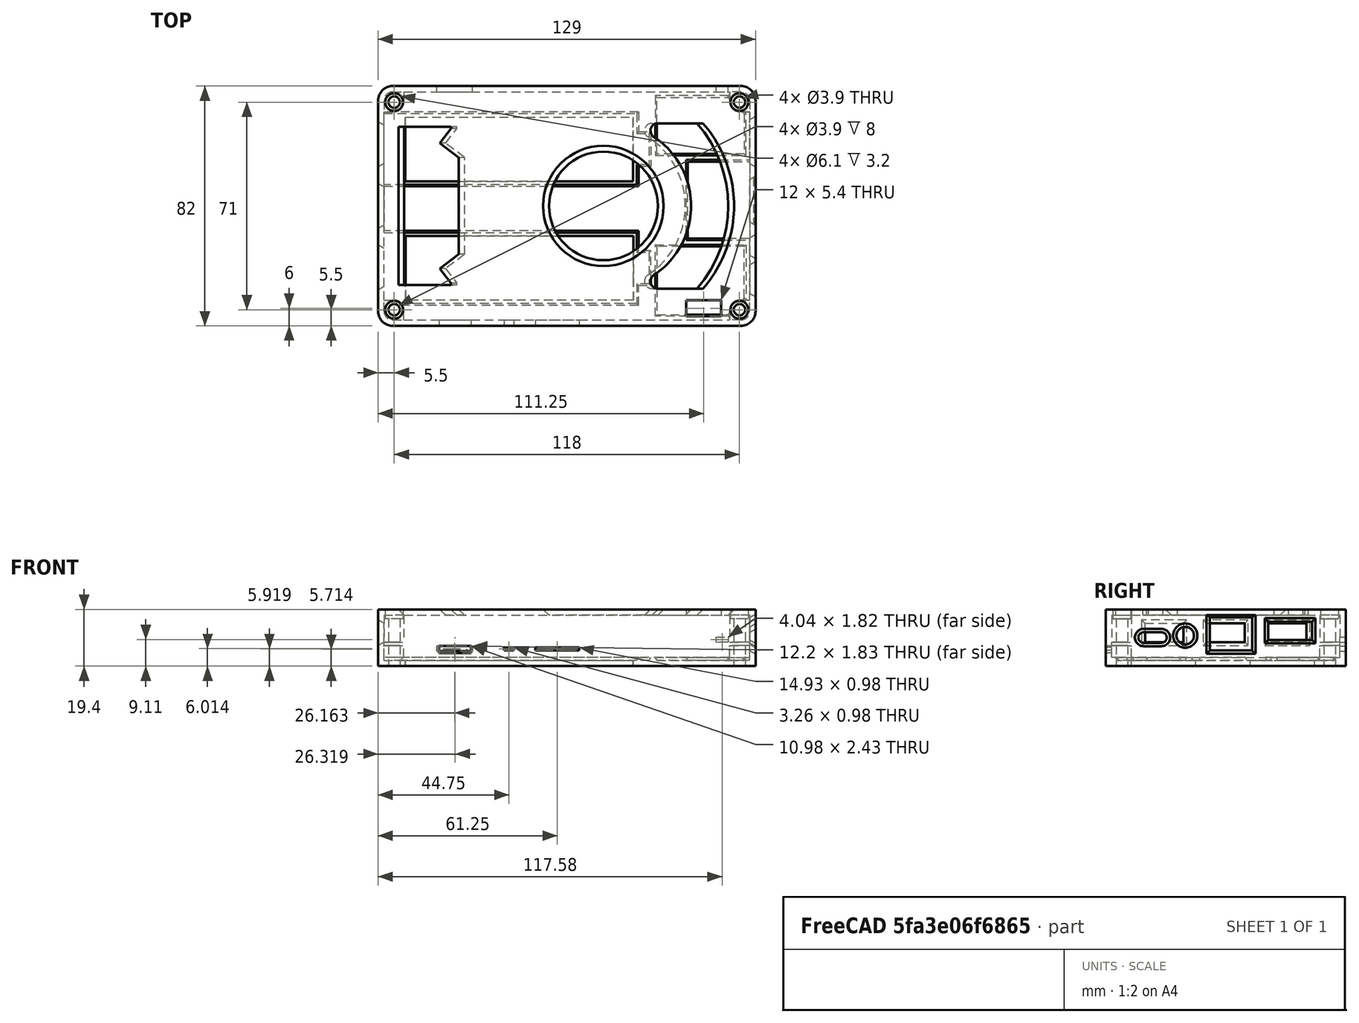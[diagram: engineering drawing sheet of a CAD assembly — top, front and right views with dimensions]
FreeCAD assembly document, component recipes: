
FREECAD ASSEMBLY — COMPONENT RECIPES ("case")

This assembly document has 10 components, labeled P0..P9 below (a component is one placed body or linked part). 4 of them carry a construction recipe — the FreeCAD feature program that regenerates the part from scratch, quoted from this document or its linked companion documents; the rest are supplied as boundary geometry only. No exploded tour is included for this assembly.
COMPONENT P0 — recipe-attached ("Parent", modeled in this document).
Construction recipe (the document's own serialized feature program — sketch geometry with constraints, then the solid features built on it; lengths are millimeters unless a unit is written):

FEATURE [Sketcher::SketchObject] Sketch  label="sketch_base"
  FullyConstrained = true
  MapMode = 5
  Support = -> [XY_Plane]
  expr: .Constraints.long_side = <<data>>.lattepanda_long + <<data>>.padding * 2
  expr: .Constraints.radius = <<data>>.lattepanda_radius
  expr: .Constraints.short_side = <<data>>.lattepanda_short + <<data>>.padding * 2
  sketch-geometry (10):
    g0: ArcOfCircle CenterX=-59.5 CenterY=36 CenterZ=0 NormalX=0 NormalY=0 NormalZ=1 AngleXU=0 Radius=3 StartAngle=1.5708 EndAngle=3.14159
    g1: LineSegment StartX=-59.5 StartY=39 StartZ=0 EndX=59.5 EndY=39 EndZ=0
    g2: ArcOfCircle CenterX=59.5 CenterY=36 CenterZ=0 NormalX=0 NormalY=0 NormalZ=1 AngleXU=0 Radius=3 StartAngle=2.097e-13 EndAngle=1.5708
    g3: LineSegment StartX=62.5 StartY=36 StartZ=0 EndX=62.5 EndY=-36 EndZ=0
    g4: ArcOfCircle CenterX=59.5 CenterY=-36 CenterZ=0 NormalX=0 NormalY=0 NormalZ=1 AngleXU=0 Radius=3 StartAngle=4.71239 EndAngle=6.28319
    g5: LineSegment StartX=59.5 StartY=-39 StartZ=0 EndX=-59.5 EndY=-39 EndZ=0
    g6: ArcOfCircle CenterX=-59.5 CenterY=-36 CenterZ=0 NormalX=0 NormalY=0 NormalZ=1 AngleXU=0 Radius=3 StartAngle=3.14159 EndAngle=4.71239
    g7: LineSegment StartX=-62.5 StartY=-36 StartZ=0 EndX=-62.5 EndY=36 EndZ=0
    g8: GeomPoint X=-62.5 Y=39 Z=0
    g9: GeomPoint X=62.5 Y=-39 Z=0
  constraints (23):
    c: Tangent(g0,g1) = 1.5708
    c: Tangent(g1,g2) = 1.5708
    c: Tangent(g2,g3) = 1.5708
    c: Tangent(g3,g4) = 1.5708
    c: Tangent(g4,g5) = 1.5708
    c: Tangent(g5,g6) = 1.5708
    c: Tangent(g6,g7) = 1.5708
    c: Tangent(g7,g0) = 1.5708
    c: Horizontal(g1)
    c: Horizontal(g5)
    c: Vertical(g3)
    c: Vertical(g7)
    c: Equal(g0,g2)
    c: Equal(g2,g4)
    c: Equal(g4,g6)
    c: PointOnObject(g8,g1)
    c: PointOnObject(g8,g7)
    c: PointOnObject(g9,g3)
    c: PointOnObject(g9,g5)
    c: DistanceY(g5,g0) = 78  'short_side'
    c: DistanceX(g0,g2) = 125  'long_side'
    c: Radius(g2) = 3  'radius'
    c: Symmetric(g0,g4,g-1)
FEATURE [PartDesign::Pad] Pad
  Direction = (0,0,1)
  Length = 15.4
  Length2 = 10
  Profile = -> Sketch
  ReferenceAxis = -> Sketch [N_Axis]
  Type = 0
  expr: Length = <<data>>.lattepanda_height
FEATURE [PartDesign::Thickness] Thickness
  Base = -> Pad [Face10]
  BaseFeature = -> Pad
  Intersection = false
  Join = 1
  Mode = 0
  SupportTransform = false
  Value = 2
  expr: Value = <<data>>.wall_thickness
FEATURE [Sketcher::SketchObject] Sketch003  label="sketch_screwhole_shafts"
  ExternalGeometry = -> [Thickness]
  FullyConstrained = true
  MapMode = 5
  Support = -> [XY_Plane]
  expr: Constraints[4] = <<data>>.screwhole_shaft_diameter + Spreadsheet.padding * 2
  expr: Constraints[68] = (<<data>>.screwhole_shaft_diameter + <<data>>.padding * 2) / 2
  expr: Constraints[8] = (<<data>>.screwhole_shaft_diameter + <<data>>.padding * 2) / 2
  sketch-geometry (24):
    g0: LineSegment StartX=-59.5 StartY=39 StartZ=0 EndX=-55.7 EndY=39 EndZ=0
    g1: LineSegment StartX=-62.5 StartY=36 StartZ=0 EndX=-62.5 EndY=32.2 EndZ=0
    g2: LineSegment StartX=-55.7 StartY=39 StartZ=0 EndX=-55.7 EndY=35.6 EndZ=0
    g3: ArcOfCircle CenterX=-59.1 CenterY=35.6 CenterZ=0 NormalX=0 NormalY=0 NormalZ=1 AngleXU=0 Radius=3.4 StartAngle=4.71239 EndAngle=6.28319
    g4: LineSegment StartX=-62.5 StartY=32.2 StartZ=0 EndX=-59.1 EndY=32.2 EndZ=0
    g5: LineSegment StartX=-59.5 StartY=-39 StartZ=0 EndX=-55.7 EndY=-39 EndZ=0
    g6: LineSegment StartX=-62.5 StartY=-36 StartZ=0 EndX=-62.5 EndY=-32.2 EndZ=0
    g7: LineSegment StartX=-55.7 StartY=-39 StartZ=0 EndX=-55.7 EndY=-35.6 EndZ=0
    g8: ArcOfCircle CenterX=-59.1 CenterY=-35.6 CenterZ=0 NormalX=0 NormalY=0 NormalZ=1 AngleXU=0 Radius=3.4 StartAngle=1e-15 EndAngle=1.5708
    g9: LineSegment StartX=-62.5 StartY=-32.2 StartZ=0 EndX=-59.1 EndY=-32.2 EndZ=0
    g10: LineSegment StartX=59.5 StartY=39 StartZ=0 EndX=55.7 EndY=39 EndZ=0
    g11: LineSegment StartX=62.5 StartY=36 StartZ=0 EndX=62.5 EndY=32.2 EndZ=0
    g12: LineSegment StartX=55.7 StartY=39 StartZ=0 EndX=55.7 EndY=35.6 EndZ=0
    g13: ArcOfCircle CenterX=59.1 CenterY=35.6 CenterZ=0 NormalX=0 NormalY=0 NormalZ=1 AngleXU=0 Radius=3.4 StartAngle=3.14159 EndAngle=4.71239
    g14: LineSegment StartX=62.5 StartY=32.2 StartZ=0 EndX=59.1 EndY=32.2 EndZ=0
    g15: LineSegment StartX=59.5 StartY=-39 StartZ=0 EndX=55.7 EndY=-39 EndZ=0
    g16: LineSegment StartX=62.5 StartY=-36 StartZ=0 EndX=62.5 EndY=-32.2 EndZ=0
    g17: LineSegment StartX=55.7 StartY=-39 StartZ=0 EndX=55.7 EndY=-35.6 EndZ=0
    g18: ArcOfCircle CenterX=59.1 CenterY=-35.6 CenterZ=0 NormalX=0 NormalY=0 NormalZ=1 AngleXU=0 Radius=3.4 StartAngle=1.5708 EndAngle=3.14159
    g19: LineSegment StartX=62.5 StartY=-32.2 StartZ=0 EndX=59.1 EndY=-32.2 EndZ=0
    g20: ArcOfCircle CenterX=-59.5 CenterY=-36 CenterZ=0 NormalX=0 NormalY=0 NormalZ=1 AngleXU=0 Radius=3 StartAngle=3.14159 EndAngle=4.71239
    g21: ArcOfCircle CenterX=-59.5 CenterY=36 CenterZ=0 NormalX=0 NormalY=0 NormalZ=1 AngleXU=0 Radius=3 StartAngle=1.5708 EndAngle=3.14159
    g22: ArcOfCircle CenterX=59.5 CenterY=36 CenterZ=0 NormalX=0 NormalY=0 NormalZ=1 AngleXU=0 Radius=3 StartAngle=2.113e-13 EndAngle=1.5708
    g23: ArcOfCircle CenterX=59.5 CenterY=-36 CenterZ=0 NormalX=0 NormalY=0 NormalZ=1 AngleXU=0 Radius=3 StartAngle=4.71239 EndAngle=6.28319
  constraints (72):
    c: Coincident(g0,g-3)
    c: Horizontal(g0)
    c: Coincident(g1,g-3)
    c: Vertical(g1)
    c: DistanceX(g1,g0) = 6.8
    c: Coincident(g2,g0)
    c: Vertical(g2)
    c: Coincident(g3,g2)
    c: Radius(g3) = 3.4
    c: Coincident(g4,g1)
    c: Coincident(g4,g3)
    c: Horizontal(g4)
    c: Equal(g1,g0)
    c: Equal(g4,g2)
    c: Horizontal(g5)
    c: Vertical(g6)
    c: Coincident(g7,g5)
    c: Vertical(g7)
    c: Coincident(g8,g7)
    c: Coincident(g9,g6)
    c: Coincident(g9,g8)
    c: Horizontal(g9)
    c: Equal(g6,g5)
    c: Equal(g9,g7)
    c: Coincident(g6,g-4)
    c: Coincident(g5,g-4)
    c: Equal(g6,g1)
    c: Equal(g9,g4)
    c: Horizontal(g10)
    c: Vertical(g11)
    c: Coincident(g12,g10)
    c: Vertical(g12)
    c: Coincident(g13,g12)
    c: Coincident(g14,g11)
    c: Coincident(g14,g13)
    c: Horizontal(g14)
    c: Equal(g11,g10)
    c: Equal(g14,g12)
    c: Horizontal(g15)
    c: Vertical(g16)
    c: Coincident(g17,g15)
    c: Vertical(g17)
    c: Coincident(g18,g17)
    c: Coincident(g19,g16)
    c: Coincident(g19,g18)
    c: Horizontal(g19)
    c: Equal(g16,g15)
    c: Equal(g19,g17)
    c: Equal(g16,g11)
    c: Equal(g19,g14)
    c: Coincident(g10,g-6)
    c: Coincident(g11,g-6)
    c: Coincident(g16,g-5)
    c: Coincident(g15,g-5)
    c: Equal(g10,g0)
    c: Coincident(g20,g-4)
    c: Coincident(g20,g5)
    c: Coincident(g20,g6)
    c: Coincident(g21,g-3)
    c: Coincident(g21,g1)
    c: Coincident(g21,g0)
    c: Coincident(g22,g-6)
    c: Coincident(g22,g10)
    c: Coincident(g22,g11)
    c: Coincident(g23,g-5)
    c: Coincident(g23,g16)
    c: Coincident(g23,g15)
    c: Equal(g17,g7)
    c: DistanceY(g2,g2) = 3.4
    c: Equal(g3,g13)
    c: Equal(g18,g8)
    c: Equal(g13,g18)
FEATURE [PartDesign::Pad] Pad001
  BaseFeature = -> Thickness
  Direction = (0,0,1)
  Length = 5
  Length2 = 10
  Profile = -> Sketch003
  ReferenceAxis = -> Sketch003 [N_Axis]
  Type = 0
  expr: Length = <<data>>.lattepanda_h_below
FEATURE [PartDesign::Body] Body  label="Parent"
  Group = -> [Sketch,Pad,Thickness,Sketch003,Pad001]
  Origin = -> Origin
  Tip = -> Pad001
COMPONENT P1 — recipe-attached ("case", modeled in this document).
Construction recipe (the document's own serialized feature program — sketch geometry with constraints, then the solid features built on it; lengths are millimeters unless a unit is written):

FEATURE [Sketcher::SketchObject] Sketch004  label="sketch_base001"
  FullyConstrained = true
  MapMode = 5
  Support = -> [XY_Plane]
  expr: .Constraints.long_side = <<data>>.lattepanda_long + <<data>>.padding * 2
  expr: .Constraints.radius = <<data>>.lattepanda_radius
  expr: .Constraints.short_side = <<data>>.lattepanda_short + <<data>>.padding * 2
  sketch-geometry (10):
    g0: ArcOfCircle CenterX=-59.5 CenterY=36 CenterZ=0 NormalX=0 NormalY=0 NormalZ=1 AngleXU=0 Radius=3 StartAngle=1.5708 EndAngle=3.14159
    g1: LineSegment StartX=-59.5 StartY=39 StartZ=0 EndX=59.5 EndY=39 EndZ=0
    g2: ArcOfCircle CenterX=59.5 CenterY=36 CenterZ=0 NormalX=0 NormalY=0 NormalZ=1 AngleXU=0 Radius=3 StartAngle=2.095e-13 EndAngle=1.5708
    g3: LineSegment StartX=62.5 StartY=36 StartZ=0 EndX=62.5 EndY=-36 EndZ=0
    g4: ArcOfCircle CenterX=59.5 CenterY=-36 CenterZ=0 NormalX=0 NormalY=0 NormalZ=1 AngleXU=0 Radius=3 StartAngle=4.71239 EndAngle=6.28319
    g5: LineSegment StartX=59.5 StartY=-39 StartZ=0 EndX=-59.5 EndY=-39 EndZ=0
    g6: ArcOfCircle CenterX=-59.5 CenterY=-36 CenterZ=0 NormalX=0 NormalY=0 NormalZ=1 AngleXU=0 Radius=3 StartAngle=3.14159 EndAngle=4.71239
    g7: LineSegment StartX=-62.5 StartY=-36 StartZ=0 EndX=-62.5 EndY=36 EndZ=0
    g8: GeomPoint X=-62.5 Y=39 Z=0
    g9: GeomPoint X=62.5 Y=-39 Z=0
  constraints (23):
    c: Tangent(g0,g1) = 1.5708
    c: Tangent(g1,g2) = 1.5708
    c: Tangent(g2,g3) = 1.5708
    c: Tangent(g3,g4) = 1.5708
    c: Tangent(g4,g5) = 1.5708
    c: Tangent(g5,g6) = 1.5708
    c: Tangent(g6,g7) = 1.5708
    c: Tangent(g7,g0) = 1.5708
    c: Horizontal(g1)
    c: Horizontal(g5)
    c: Vertical(g3)
    c: Vertical(g7)
    c: Equal(g0,g2)
    c: Equal(g2,g4)
    c: Equal(g4,g6)
    c: PointOnObject(g8,g1)
    c: PointOnObject(g8,g7)
    c: PointOnObject(g9,g3)
    c: PointOnObject(g9,g5)
    c: DistanceY(g5,g0) = 78  'short_side'
    c: DistanceX(g0,g2) = 125  'long_side'
    c: Radius(g2) = 3  'radius'
    c: Symmetric(g0,g4,g-1)
FEATURE [PartDesign::Pad] Pad002
  Direction = (0,0,1)
  Length = 15.4
  Length2 = 10
  Profile = -> Sketch004
  ReferenceAxis = -> Sketch004 [N_Axis]
  Type = 0
  expr: Length = <<data>>.lattepanda_height
FEATURE [PartDesign::Thickness] Thickness001
  Base = -> Pad002 [Face10]
  BaseFeature = -> Pad002
  Intersection = false
  Join = 1
  Mode = 0
  SupportTransform = false
  Value = 2
  expr: Value = <<data>>.wall_thickness
FEATURE [Sketcher::SketchObject] Sketch005  label="sketch_screwhole_shafts001"
  ExternalGeometry = -> [Thickness001]
  FullyConstrained = true
  MapMode = 5
  Support = -> [XY_Plane]
  expr: Constraints[4] = <<data>>.screwhole_shaft_diameter + Spreadsheet.padding * 2
  expr: Constraints[68] = (<<data>>.screwhole_shaft_diameter + <<data>>.padding * 2) / 2
  expr: Constraints[8] = (<<data>>.screwhole_shaft_diameter + <<data>>.padding * 2) / 2
  sketch-geometry (24):
    g0: LineSegment StartX=-59.5 StartY=39 StartZ=0 EndX=-55.7 EndY=39 EndZ=0
    g1: LineSegment StartX=-62.5 StartY=36 StartZ=0 EndX=-62.5 EndY=32.2 EndZ=0
    g2: LineSegment StartX=-55.7 StartY=39 StartZ=0 EndX=-55.7 EndY=35.6 EndZ=0
    g3: ArcOfCircle CenterX=-59.1 CenterY=35.6 CenterZ=0 NormalX=0 NormalY=0 NormalZ=1 AngleXU=0 Radius=3.4 StartAngle=4.71239 EndAngle=6.28319
    g4: LineSegment StartX=-62.5 StartY=32.2 StartZ=0 EndX=-59.1 EndY=32.2 EndZ=0
    g5: LineSegment StartX=-59.5 StartY=-39 StartZ=0 EndX=-55.7 EndY=-39 EndZ=0
    g6: LineSegment StartX=-62.5 StartY=-36 StartZ=0 EndX=-62.5 EndY=-32.2 EndZ=0
    g7: LineSegment StartX=-55.7 StartY=-39 StartZ=0 EndX=-55.7 EndY=-35.6 EndZ=0
    g8: ArcOfCircle CenterX=-59.1 CenterY=-35.6 CenterZ=0 NormalX=0 NormalY=0 NormalZ=1 AngleXU=0 Radius=3.4 StartAngle=-2.7e-15 EndAngle=1.5708
    g9: LineSegment StartX=-62.5 StartY=-32.2 StartZ=0 EndX=-59.1 EndY=-32.2 EndZ=0
    g10: LineSegment StartX=59.5 StartY=39 StartZ=0 EndX=55.7 EndY=39 EndZ=0
    g11: LineSegment StartX=62.5 StartY=36 StartZ=0 EndX=62.5 EndY=32.2 EndZ=0
    g12: LineSegment StartX=55.7 StartY=39 StartZ=0 EndX=55.7 EndY=35.6 EndZ=0
    g13: ArcOfCircle CenterX=59.1 CenterY=35.6 CenterZ=0 NormalX=0 NormalY=0 NormalZ=1 AngleXU=0 Radius=3.4 StartAngle=3.14159 EndAngle=4.71239
    g14: LineSegment StartX=62.5 StartY=32.2 StartZ=0 EndX=59.1 EndY=32.2 EndZ=0
    g15: LineSegment StartX=59.5 StartY=-39 StartZ=0 EndX=55.7 EndY=-39 EndZ=0
    g16: LineSegment StartX=62.5 StartY=-36 StartZ=0 EndX=62.5 EndY=-32.2 EndZ=0
    g17: LineSegment StartX=55.7 StartY=-39 StartZ=0 EndX=55.7 EndY=-35.6 EndZ=0
    g18: ArcOfCircle CenterX=59.1 CenterY=-35.6 CenterZ=0 NormalX=0 NormalY=0 NormalZ=1 AngleXU=0 Radius=3.4 StartAngle=1.5708 EndAngle=3.14159
    g19: LineSegment StartX=62.5 StartY=-32.2 StartZ=0 EndX=59.1 EndY=-32.2 EndZ=0
    g20: ArcOfCircle CenterX=-59.5 CenterY=-36 CenterZ=0 NormalX=0 NormalY=0 NormalZ=1 AngleXU=0 Radius=3 StartAngle=3.14159 EndAngle=4.71239
    g21: ArcOfCircle CenterX=-59.5 CenterY=36 CenterZ=0 NormalX=0 NormalY=0 NormalZ=1 AngleXU=0 Radius=3 StartAngle=1.5708 EndAngle=3.14159
    g22: ArcOfCircle CenterX=59.5 CenterY=36 CenterZ=0 NormalX=0 NormalY=0 NormalZ=1 AngleXU=0 Radius=3 StartAngle=2.089e-13 EndAngle=1.5708
    g23: ArcOfCircle CenterX=59.5 CenterY=-36 CenterZ=0 NormalX=0 NormalY=0 NormalZ=1 AngleXU=0 Radius=3 StartAngle=4.71239 EndAngle=6.28319
  constraints (72):
    c: Coincident(g0,g-3)
    c: Horizontal(g0)
    c: Coincident(g1,g-3)
    c: Vertical(g1)
    c: DistanceX(g1,g0) = 6.8
    c: Coincident(g2,g0)
    c: Vertical(g2)
    c: Coincident(g3,g2)
    c: Radius(g3) = 3.4
    c: Coincident(g4,g1)
    c: Coincident(g4,g3)
    c: Horizontal(g4)
    c: Equal(g1,g0)
    c: Equal(g4,g2)
    c: Horizontal(g5)
    c: Vertical(g6)
    c: Coincident(g7,g5)
    c: Vertical(g7)
    c: Coincident(g8,g7)
    c: Coincident(g9,g6)
    c: Coincident(g9,g8)
    c: Horizontal(g9)
    c: Equal(g6,g5)
    c: Equal(g9,g7)
    c: Coincident(g6,g-4)
    c: Coincident(g5,g-4)
    c: Equal(g6,g1)
    c: Equal(g9,g4)
    c: Horizontal(g10)
    c: Vertical(g11)
    c: Coincident(g12,g10)
    c: Vertical(g12)
    c: Coincident(g13,g12)
    c: Coincident(g14,g11)
    c: Coincident(g14,g13)
    c: Horizontal(g14)
    c: Equal(g11,g10)
    c: Equal(g14,g12)
    c: Horizontal(g15)
    c: Vertical(g16)
    c: Coincident(g17,g15)
    c: Vertical(g17)
    c: Coincident(g18,g17)
    c: Coincident(g19,g16)
    c: Coincident(g19,g18)
    c: Horizontal(g19)
    c: Equal(g16,g15)
    c: Equal(g19,g17)
    c: Equal(g16,g11)
    c: Equal(g19,g14)
    c: Coincident(g10,g-6)
    c: Coincident(g11,g-6)
    c: Coincident(g16,g-5)
    c: Coincident(g15,g-5)
    c: Equal(g10,g0)
    c: Coincident(g20,g-4)
    c: Coincident(g20,g5)
    c: Coincident(g20,g6)
    c: Coincident(g21,g-3)
    c: Coincident(g21,g1)
    c: Coincident(g21,g0)
    c: Coincident(g22,g-6)
    c: Coincident(g22,g10)
    c: Coincident(g22,g11)
    c: Coincident(g23,g-5)
    c: Coincident(g23,g16)
    c: Coincident(g23,g15)
    c: Equal(g17,g7)
    c: DistanceY(g2,g2) = 3.4
    c: Equal(g3,g13)
    c: Equal(g18,g8)
    c: Equal(g13,g18)
FEATURE [PartDesign::Pad] Pad003
  BaseFeature = -> Thickness001
  Direction = (0,0,1)
  Length = 5
  Length2 = 10
  Profile = -> Sketch005
  ReferenceAxis = -> Sketch005 [N_Axis]
  Type = 0
  expr: Length = <<data>>.lattepanda_h_below
FEATURE [Sketcher::SketchObject] Sketch007
  ExternalGeometry = -> [Feature]
  FullyConstrained = true
  MapMode = 5
  Placement = pos=(62.5,0,0) rot=(0.57735,-0.57735,-0.57735;2.0944rad)
  Support = -> [Pad003]
  sketch-geometry (24):
    g0: GeomPoint X=13.85 Y=8.45 Z=0
    g1: GeomPoint X=28.1 Y=7.78 Z=0
    g2: GeomPoint X=21.96 Y=7.78 Z=0
    g3: LineSegment StartX=21.96 StartY=9.58 StartZ=0 EndX=28.1 EndY=9.58 EndZ=0
    g4: LineSegment StartX=21.96 StartY=5.98 StartZ=0 EndX=28.1 EndY=5.98 EndZ=0
    g5: GeomPoint X=5.4559 Y=14.6873 Z=0
    g6: GeomPoint X=5.4559 Y=3.34 Z=0
    g7: GeomPoint X=-9.04069 Y=3.34 Z=0
    g8: GeomPoint X=-9.04069 Y=14.6873 Z=0
    g9: LineSegment StartX=5.4559 StartY=14.6873 StartZ=0 EndX=-9.04069 EndY=14.6873 EndZ=0
    g10: LineSegment StartX=-9.04069 StartY=3.34 StartZ=0 EndX=-9.04069 EndY=14.6873 EndZ=0
    g11: LineSegment StartX=-9.04069 StartY=3.34 StartZ=0 EndX=5.4559 EndY=3.34 EndZ=0
    g12: LineSegment StartX=5.4559 StartY=3.34 StartZ=0 EndX=5.4559 EndY=14.6873 EndZ=0
    g13: GeomPoint X=-14.5 Y=13.2209 Z=0
    g14: GeomPoint X=-14.5 Y=6.95627 Z=0
    g15: GeomPoint X=-29.5 Y=6.95627 Z=0
    g16: GeomPoint X=-29.5 Y=13.2209 Z=0
    g17: LineSegment StartX=-14.5 StartY=13.2209 StartZ=0 EndX=-29.5 EndY=13.2209 EndZ=0
    g18: LineSegment StartX=-29.5 StartY=13.2209 StartZ=0 EndX=-29.5 EndY=6.95627 EndZ=0
    g19: LineSegment StartX=-29.5 StartY=6.95627 StartZ=0 EndX=-14.5 EndY=6.95627 EndZ=0
    g20: LineSegment StartX=-14.5 StartY=6.95627 StartZ=0 EndX=-14.5 EndY=13.2209 EndZ=0
    g21: ArcOfCircle CenterX=21.96 CenterY=7.78 CenterZ=0 NormalX=0 NormalY=0 NormalZ=1 AngleXU=0 Radius=1.8 StartAngle=1.5708 EndAngle=4.71239
    g22: ArcOfCircle CenterX=28.1 CenterY=7.78 CenterZ=0 NormalX=0 NormalY=0 NormalZ=1 AngleXU=0 Radius=1.8 StartAngle=4.71239 EndAngle=7.85398
    g23: Circle CenterX=13.85 CenterY=8.45 CenterZ=0 NormalX=0 NormalY=0 NormalZ=1 AngleXU=0 Radius=3
  constraints (50):
    c: Symmetric(g-12,g-12,g0)
    c: Horizontal(g1,g2)
    c: Vertical(g2,g-17)
    c: Symmetric(g-15,g-14,g1)
    c: Horizontal(g3)
    c: Horizontal(g4)
    c: Equal(g4,g3)
    c: Horizontal(g5,g-5)
    c: Vertical(g5,g-3)
    c: Horizontal(g8,g-5)
    c: Vertical(g8,g-4)
    c: Vertical(g7,g-4)
    c: Vertical(g6,g-3)
    c: Horizontal(g6,g7)
    c: Horizontal(g7,g-6)
    c: Coincident(g9,g5)
    c: Coincident(g9,g8)
    c: Coincident(g10,g7)
    c: Coincident(g10,g9)
    c: Coincident(g11,g10)
    c: Coincident(g11,g6)
    c: Coincident(g12,g11)
    c: Coincident(g12,g9)
    c: Horizontal(g13,g-7)
    c: Horizontal(g-7,g16)
    c: Horizontal(g15,g-9)
    c: Horizontal(g-9,g14)
    c: Vertical(g13,g-8)
    c: Vertical(g-8,g14)
    c: Vertical(g16,g-10)
    c: Vertical(g-10,g15)
    c: Coincident(g17,g13)
    c: Coincident(g17,g16)
    c: Coincident(g18,g17)
    c: Coincident(g18,g15)
    c: Coincident(g19,g18)
    c: Coincident(g19,g14)
    c: Coincident(g20,g19)
    c: Coincident(g20,g17)
    c: Coincident(g21,g2)
    c: Coincident(g21,g4)
    c: Coincident(g21,g3)
    c: Coincident(g22,g1)
    c: Coincident(g22,g3)
    c: Coincident(g22,g4)
    c: Equal(g21,g22)
    c: Angle(g22) = 3.14159
    c: Radius(g22) = 1.8
    c: Coincident(g23,g0)
    c: Radius(g23) = 3
FEATURE [PartDesign::Pocket] Pocket
  BaseFeature = -> Pad003
  Direction = (1,0,0)
  Length = 5
  Length2 = 5
  Profile = -> Sketch007
  ReferenceAxis = -> Sketch007 [N_Axis]
  TaperAngle = 30
  Type = 0
FEATURE [Sketcher::SketchObject] Sketch009
  ExternalGeometry = -> [Feature]
  FullyConstrained = true
  MapMode = 5
  Placement = pos=(-62.5,0,0) rot=(0.57735,0.57735,0.57735;2.0944rad)
  Support = -> [Pocket]
  sketch-geometry (12):
    g0: LineSegment StartX=-27.6 StartY=12.6565 StartZ=0 EndX=-14.5 EndY=12.6565 EndZ=0
    g1: LineSegment StartX=-14.5 StartY=12.6565 StartZ=0 EndX=-14.5 EndY=6.2 EndZ=0
    g2: LineSegment StartX=-14.5 StartY=6.2 StartZ=0 EndX=-27.6 EndY=6.2 EndZ=0
    g3: LineSegment StartX=-27.6 StartY=6.2 StartZ=0 EndX=-27.6 EndY=12.6565 EndZ=0
    g4: LineSegment StartX=-6.60005 StartY=12.6565 StartZ=0 EndX=6.49995 EndY=12.6565 EndZ=0
    g5: LineSegment StartX=6.49995 StartY=12.6565 StartZ=0 EndX=6.49995 EndY=6.2 EndZ=0
    g6: LineSegment StartX=6.49995 StartY=6.2 StartZ=0 EndX=-6.60005 EndY=6.2 EndZ=0
    g7: LineSegment StartX=-6.60005 StartY=6.2 StartZ=0 EndX=-6.60005 EndY=12.6565 EndZ=0
    g8: LineSegment StartX=14.5 StartY=12.6565 StartZ=0 EndX=27.6 EndY=12.6565 EndZ=0
    g9: LineSegment StartX=27.6 StartY=12.6565 StartZ=0 EndX=27.6 EndY=6.2 EndZ=0
    g10: LineSegment StartX=27.6 StartY=6.2 StartZ=0 EndX=14.5 EndY=6.2 EndZ=0
    g11: LineSegment StartX=14.5 StartY=6.2 StartZ=0 EndX=14.5 EndY=12.6565 EndZ=0
  constraints (36):
    c: Coincident(g0,g1)
    c: Coincident(g1,g2)
    c: Coincident(g2,g3)
    c: Coincident(g3,g0)
    c: Horizontal(g0)
    c: Horizontal(g2)
    c: Vertical(g1)
    c: Vertical(g3)
    c: Horizontal(g0,g-13)
    c: Vertical(g0,g-17)
    c: Vertical(g1,g-14)
    c: Horizontal(g1,g-15)
    c: Coincident(g4,g5)
    c: Coincident(g5,g6)
    c: Coincident(g6,g7)
    c: Coincident(g7,g4)
    c: Horizontal(g4)
    c: Horizontal(g6)
    c: Vertical(g5)
    c: Vertical(g7)
    c: Coincident(g8,g9)
    c: Coincident(g9,g10)
    c: Coincident(g10,g11)
    c: Coincident(g11,g8)
    c: Horizontal(g8)
    c: Horizontal(g10)
    c: Vertical(g9)
    c: Vertical(g11)
    c: Vertical(g8,g-5)
    c: Horizontal(g8,g-4)
    c: Vertical(g9,g-3)
    c: Horizontal(g-6,g9)
    c: Vertical(g5,g-9)
    c: Horizontal(g-10,g5)
    c: Horizontal(g4,g-8)
    c: Vertical(g4,g-12)
FEATURE [PartDesign::Pocket] Pocket001
  BaseFeature = -> Pocket
  Direction = (-1,0,0)
  Length = 5
  Length2 = 5
  Profile = -> Sketch009
  ReferenceAxis = -> Sketch009 [N_Axis]
  TaperAngle = 30
  Type = 0
FEATURE [Sketcher::SketchObject] Sketch010
  ExternalGeometry = -> [Feature]
  FullyConstrained = true
  MapMode = 5
  Placement = pos=(0,-39,0) rot=(0,0.707107,0.707107;3.14159rad)
  Support = -> [Pocket001]
  sketch-geometry (12):
    g0: LineSegment StartX=21.3778 StartY=4.409 StartZ=0 EndX=18.1222 EndY=4.409 EndZ=0
    g1: LineSegment StartX=18.1222 StartY=4.409 StartZ=0 EndX=18.1222 EndY=3.429 EndZ=0
    g2: LineSegment StartX=18.1222 StartY=3.429 StartZ=0 EndX=21.3778 EndY=3.429 EndZ=0
    g3: LineSegment StartX=21.3778 StartY=3.429 StartZ=0 EndX=21.3778 EndY=4.409 EndZ=0
    g4: LineSegment StartX=10.7144 StartY=4.409 StartZ=0 EndX=-4.2144 EndY=4.409 EndZ=0
    g5: LineSegment StartX=-4.2144 StartY=4.409 StartZ=0 EndX=-4.2144 EndY=3.429 EndZ=0
    g6: LineSegment StartX=-4.2144 StartY=3.429 StartZ=0 EndX=10.7144 EndY=3.429 EndZ=0
    g7: LineSegment StartX=10.7144 StartY=3.429 StartZ=0 EndX=10.7144 EndY=4.409 EndZ=0
    g8: LineSegment StartX=43.6699 StartY=4.92863 StartZ=0 EndX=32.6928 EndY=4.92863 EndZ=0
    g9: LineSegment StartX=32.6928 StartY=4.92863 StartZ=0 EndX=32.6928 EndY=2.49861 EndZ=0
    g10: LineSegment StartX=32.6928 StartY=2.49861 StartZ=0 EndX=43.6699 EndY=2.49861 EndZ=0
    g11: LineSegment StartX=43.6699 StartY=2.49861 StartZ=0 EndX=43.6699 EndY=4.92863 EndZ=0
  constraints (30):
    c: Coincident(g0,g1)
    c: Coincident(g1,g2)
    c: Coincident(g2,g3)
    c: Coincident(g3,g0)
    c: Horizontal(g0)
    c: Horizontal(g2)
    c: Vertical(g1)
    c: Vertical(g3)
    c: Coincident(g0,g-14)
    c: Coincident(g1,g-5)
    c: Coincident(g4,g5)
    c: Coincident(g5,g6)
    c: Coincident(g6,g7)
    c: Coincident(g7,g4)
    c: Horizontal(g4)
    c: Horizontal(g6)
    c: Vertical(g5)
    c: Vertical(g7)
    c: Coincident(g4,g-11)
    c: Coincident(g5,g-6)
    c: Coincident(g8,g9)
    c: Coincident(g9,g10)
    c: Coincident(g10,g11)
    c: Coincident(g11,g8)
    c: Horizontal(g8)
    c: Horizontal(g10)
    c: Vertical(g9)
    c: Vertical(g11)
    c: Coincident(g8,g-15)
    c: Coincident(g9,g-16)
FEATURE [PartDesign::Pocket] Pocket002
  BaseFeature = -> Pocket001
  Direction = (0,-1,2e-16)
  Length = 5
  Length2 = 5
  Profile = -> Sketch010
  ReferenceAxis = -> Sketch010 [N_Axis]
  Type = 0
FEATURE [Sketcher::SketchObject] Sketch012
  ExternalGeometry = -> [Feature]
  FullyConstrained = true
  MapMode = 5
  Placement = pos=(0,39,0) rot=(1,0,0;1.5708rad)
  Support = -> [Pocket002]
  sketch-geometry (8):
    g0: LineSegment StartX=-44.4383 StartY=4.92863 StartZ=0 EndX=-32.2351 EndY=4.92863 EndZ=0
    g1: LineSegment StartX=-32.2351 StartY=4.92863 StartZ=0 EndX=-32.2351 EndY=3.09856 EndZ=0
    g2: LineSegment StartX=-32.2351 StartY=3.09856 StartZ=0 EndX=-44.4383 EndY=3.09856 EndZ=0
    g3: LineSegment StartX=-44.4383 StartY=3.09856 StartZ=0 EndX=-44.4383 EndY=4.92863 EndZ=0
    g4: LineSegment StartX=51.06 StartY=8.02 StartZ=0 EndX=55.1 EndY=8.02 EndZ=0
    g5: LineSegment StartX=55.1 StartY=8.02 StartZ=0 EndX=55.1 EndY=6.2 EndZ=0
    g6: LineSegment StartX=55.1 StartY=6.2 StartZ=0 EndX=51.06 EndY=6.2 EndZ=0
    g7: LineSegment StartX=51.06 StartY=6.2 StartZ=0 EndX=51.06 EndY=8.02 EndZ=0
  constraints (21):
    c: Coincident(g0,g1)
    c: Coincident(g1,g2)
    c: Coincident(g2,g3)
    c: Coincident(g3,g0)
    c: Horizontal(g0)
    c: Horizontal(g2)
    c: Vertical(g1)
    c: Vertical(g3)
    c: Coincident(g0,g-12)
    c: Vertical(g1,g-11)
    c: Horizontal(g-10,g1)
    c: Coincident(g4,g5)
    c: Coincident(g5,g6)
    c: Coincident(g6,g7)
    c: Coincident(g7,g4)
    c: Horizontal(g4)
    c: Horizontal(g6)
    c: Vertical(g5)
    c: Vertical(g7)
    c: Coincident(g4,g-7)
    c: Coincident(g5,g-9)
FEATURE [PartDesign::Pocket] Pocket003
  BaseFeature = -> Pocket002
  Direction = (0,1,-2e-16)
  Length = 5
  Length2 = 5
  Profile = -> Sketch012
  ReferenceAxis = -> Sketch012 [N_Axis]
  Type = 0
FEATURE [Sketcher::SketchObject] Sketch014
  ExternalGeometry = -> [Feature]
  FullyConstrained = true
  MapMode = 5
  Placement = pos=(0,0,-2) rot=(1,0,0;3.14159rad)
  Support = -> [Pocket003]
  sketch-geometry (8):
    g0: LineSegment StartX=22.7645 StartY=10.2697 StartZ=0 EndX=-55.0855 EndY=10.2697 EndZ=0
    g1: LineSegment StartX=-55.0855 StartY=10.2697 StartZ=0 EndX=-55.0855 EndY=32.2697 EndZ=0
    g2: LineSegment StartX=-55.0855 StartY=32.2697 StartZ=0 EndX=22.7645 EndY=32.2697 EndZ=0
    g3: LineSegment StartX=22.7645 StartY=32.2697 StartZ=0 EndX=22.7645 EndY=10.2697 EndZ=0
    g4: LineSegment StartX=22.6499 StartY=-30.4249 StartZ=0 EndX=-55.2001 EndY=-30.4249 EndZ=0
    g5: LineSegment StartX=-55.2001 StartY=-30.4249 StartZ=0 EndX=-55.2001 EndY=-8.42495 EndZ=0
    g6: LineSegment StartX=-55.2001 StartY=-8.42495 StartZ=0 EndX=22.6499 EndY=-8.42495 EndZ=0
    g7: LineSegment StartX=22.6499 StartY=-8.42495 StartZ=0 EndX=22.6499 EndY=-30.4249 EndZ=0
  constraints (22):
    c: Coincident(g0,g1)
    c: Coincident(g1,g2)
    c: Coincident(g2,g3)
    c: Coincident(g3,g0)
    c: Horizontal(g0)
    c: Horizontal(g2)
    c: Vertical(g1)
    c: Vertical(g3)
    c: Coincident(g0,g-5)
    c: Coincident(g4,g5)
    c: Coincident(g5,g6)
    c: Coincident(g6,g7)
    c: Coincident(g7,g4)
    c: Horizontal(g4)
    c: Horizontal(g6)
    c: Vertical(g5)
    c: Vertical(g7)
    c: Coincident(g4,g-8)
    c: Vertical(g5,g-4)
    c: Horizontal(g5,g-7)
    c: Vertical(g1,g-3)
    c: Horizontal(g1,g-6)
FEATURE [PartDesign::Pocket] Pocket004
  BaseFeature = -> Pocket003
  Direction = (0,0,1)
  Length = 5
  Length2 = 5
  Profile = -> Sketch014
  ReferenceAxis = -> Sketch014 [N_Axis]
  Type = 0
FEATURE [Sketcher::SketchObject] Sketch015
  ExternalGeometry = -> [Pocket004]
  FullyConstrained = true
  MapMode = 5
  Placement = pos=(0,0,-2) rot=(1,0,0;3.14159rad)
  Support = -> [Pocket004]
  sketch-geometry (42):
    g0: LineSegment StartX=22.7645 StartY=10.2697 StartZ=0 EndX=-64.5 EndY=10.2697 EndZ=0
    g1: LineSegment StartX=-64.5 StartY=10.2697 StartZ=0 EndX=-64.5 EndY=-8.42495 EndZ=0
    g2: LineSegment StartX=-64.5 StartY=-8.42495 StartZ=0 EndX=22.7645 EndY=-8.42495 EndZ=0
    g3: LineSegment StartX=-64.5 StartY=-36 StartZ=0 EndX=-59.5 EndY=-41 EndZ=0
    g4: LineSegment StartX=42.5 StartY=10 StartZ=0 EndX=42.5 EndY=-14 EndZ=0
    g5: LineSegment StartX=59.5 StartY=41 StartZ=0 EndX=64.5 EndY=36 EndZ=0
    g6: LineSegment StartX=59.5 StartY=-41 StartZ=0 EndX=64.5 EndY=-36 EndZ=0
    g7: LineSegment StartX=42.5 StartY=10 StartZ=0 EndX=64.5 EndY=10 EndZ=0
    g8: LineSegment StartX=42.5 StartY=-14 StartZ=0 EndX=64.5 EndY=-14 EndZ=0
    g9: LineSegment StartX=-59.5 StartY=41 StartZ=0 EndX=59.5 EndY=41 EndZ=0
    g10: LineSegment StartX=22.7645 StartY=32.2697 StartZ=0 EndX=22.7645 EndY=25.4697 EndZ=0
    g11: LineSegment StartX=22.7645 StartY=25.4697 StartZ=0 EndX=26.9645 EndY=25.4697 EndZ=0
    g12: LineSegment StartX=26.9645 StartY=17.0697 StartZ=0 EndX=22.7645 EndY=17.0697 EndZ=0
    g13: LineSegment StartX=22.7645 StartY=17.0697 StartZ=0 EndX=22.7645 EndY=10.2697 EndZ=0
    g14: LineSegment StartX=26.9645 StartY=25.4697 StartZ=0 EndX=26.9645 EndY=17.0697 EndZ=0
    g15: LineSegment StartX=64.5 StartY=36 StartZ=0 EndX=64.5 EndY=10 EndZ=0
    g16: LineSegment StartX=-59.5 StartY=-41 StartZ=0 EndX=59.5 EndY=-41 EndZ=0
    g17: LineSegment StartX=64.5 StartY=-14 StartZ=0 EndX=64.5 EndY=-36 EndZ=0
    g18: LineSegment StartX=22.7645 StartY=-8.42495 StartZ=0 EndX=22.7645 EndY=-15.2249 EndZ=0
    g19: LineSegment StartX=22.7645 StartY=-30.4249 StartZ=0 EndX=22.7645 EndY=-23.6249 EndZ=0
    g20: LineSegment StartX=22.7645 StartY=-23.6249 StartZ=0 EndX=26.9645 EndY=-23.6249 EndZ=0
    g21: LineSegment StartX=26.9645 StartY=-23.6249 StartZ=0 EndX=26.9645 EndY=-15.2249 EndZ=0
    g22: LineSegment StartX=26.9645 StartY=-15.2249 StartZ=0 EndX=22.7645 EndY=-15.2249 EndZ=0
    g23: LineSegment StartX=-59.5 StartY=41 StartZ=0 EndX=-64.5 EndY=36 EndZ=0
    g24: LineSegment StartX=22.7645 StartY=32.2697 StartZ=0 EndX=-64.5 EndY=32.2697 EndZ=0
    g25: LineSegment StartX=-64.5 StartY=32.2697 StartZ=0 EndX=-64.5 EndY=36 EndZ=0
    g26: LineSegment StartX=22.7645 StartY=-30.4249 StartZ=0 EndX=-64.5 EndY=-30.4249 EndZ=0
    g27: LineSegment StartX=-64.5 StartY=-30.4249 StartZ=0 EndX=-64.5 EndY=-36 EndZ=0
    g28: LineSegment StartX=31.9645 StartY=36 StartZ=0 EndX=31.9645 EndY=15 EndZ=0
    g29: LineSegment StartX=31.9645 StartY=15 StartZ=0 EndX=59.5 EndY=15 EndZ=0
    g30: LineSegment StartX=59.5 StartY=15 StartZ=0 EndX=59.5 EndY=31 EndZ=0
    g31: LineSegment StartX=59.5 StartY=31 StartZ=0 EndX=54.5 EndY=36 EndZ=0
    g32: LineSegment StartX=54.5 StartY=36 StartZ=0 EndX=31.9645 EndY=36 EndZ=0
    g33: LineSegment StartX=31.9645 StartY=-19 StartZ=0 EndX=59.5 EndY=-19 EndZ=0
    g34: LineSegment StartX=59.5 StartY=-19 StartZ=0 EndX=59.5 EndY=-31 EndZ=0
    g35: LineSegment StartX=59.5 StartY=-31 StartZ=0 EndX=54.5 EndY=-36 EndZ=0
    g36: LineSegment StartX=54.5 StartY=-36 StartZ=0 EndX=31.9645 EndY=-36 EndZ=0
    g37: LineSegment StartX=31.9645 StartY=-36 StartZ=0 EndX=31.9645 EndY=-19 EndZ=0
    g38: LineSegment StartX=-55.0855 StartY=5.26966 StartZ=0 EndX=31.9645 EndY=5.26966 EndZ=0
    g39: LineSegment StartX=31.9645 StartY=5.26966 StartZ=0 EndX=31.9645 EndY=-3.42495 EndZ=0
    g40: LineSegment StartX=31.9645 StartY=-3.42495 StartZ=0 EndX=-55.0855 EndY=-3.42495 EndZ=0
    g41: LineSegment StartX=-55.0855 StartY=-3.42495 StartZ=0 EndX=-55.0855 EndY=5.26966 EndZ=0
  constraints (116):
    c: Coincident(g0,g1)
    c: Coincident(g1,g2)
    c: Horizontal(g0)
    c: Horizontal(g2)
    c: Vertical(g1)
    c: Coincident(g0,g-9)
    c: PointOnObject(g1,g-3)
    c: Horizontal(g1,g-8)
    c: Vertical(g4)
    c: Coincident(g5,g-5)
    c: Coincident(g6,g-5)
    c: Coincident(g7,g4)
    c: Horizontal(g7)
    c: Coincident(g8,g4)
    c: Horizontal(g8)
    c: Equal(g2,g0)
    c: Vertical(g19,g2)
    c: Horizontal(g-7,g19)
    c: Coincident(g9,g5)
    c: Vertical(g10)
    c: Coincident(g11,g10)
    c: Horizontal(g11)
    c: Horizontal(g12)
    c: Coincident(g13,g12)
    c: Coincident(g13,g0)
    c: Vertical(g13)
    c: Equal(g10,g13)
    c: Coincident(g10,g-10)
    c: Coincident(g14,g11)
    c: Coincident(g14,g12)
    c: Vertical(g14)
    c: DistanceY(g14,g14) = 8.4
    c: DistanceX(g11,g11) = 4.2
    c: Coincident(g5,g-4)
    c: Coincident(g15,g5)
    c: Coincident(g15,g7)
    c: Vertical(g15)
    c: Coincident(g3,g-6)
    c: Coincident(g16,g3)
    c: Coincident(g16,g6)
    c: Coincident(g6,g-6)
    c: Coincident(g17,g8)
    c: Coincident(g17,g6)
    c: Vertical(g17)
    c: Coincident(g18,g2)
    c: Vertical(g18)
    c: Vertical(g19)
    c: Coincident(g20,g19)
    c: Horizontal(g20)
    c: Vertical(g21)
    c: Coincident(g22,g18)
    c: Horizontal(g22)
    c: Equal(g18,g19)
    c: Equal(g19,g13)
    c: Equal(g22,g12)
    c: Coincident(g21,g22)
    c: Coincident(g21,g20)
    c: DistanceY(g15,g15) = 26
    c: DistanceY(g17,g17) = 22
    c: DistanceX(g7,g7) = 22
    c: Coincident(g23,g9)
    c: Coincident(g23,g-3)
    c: Coincident(g24,g10)
    c: Coincident(g25,g24)
    c: Coincident(g25,g23)
    c: Vertical(g25)
    c: Horizontal(g24)
    c: Coincident(g9,g-4)
    c: Coincident(g3,g-3)
    c: Coincident(g26,g19)
    c: PointOnObject(g26,g-3)
    c: Horizontal(g26)
    c: Coincident(g27,g26)
    c: Coincident(g27,g3)
    c: Vertical(g28)
    c: Coincident(g29,g28)
    c: Horizontal(g29)
    c: Coincident(g30,g29)
    c: Coincident(g31,g30)
    c: Coincident(g32,g31)
    c: Coincident(g32,g28)
    c: Horizontal(g32)
    c: Vertical(g30)
    c: DistanceY(g7,g29) = 5
    c: DistanceY(g31,g5) = 5
    c: DistanceY(g30,g5) = 5
    c: DistanceX(g31,g5) = 5
    c: DistanceX(g30,g5) = 5
    c: DistanceX(g12,g28) = 5
    c: Horizontal(g33)
    c: Coincident(g34,g33)
    c: Vertical(g34)
    c: Coincident(g35,g34)
    c: Coincident(g36,g35)
    c: Horizontal(g36)
    c: Coincident(g37,g36)
    c: Coincident(g37,g33)
    c: DistanceX(g20,g33) = 5
    c: Vertical(g37)
    c: DistanceY(g6,g35) = 5
    c: DistanceX(g35,g6) = 5
    c: DistanceX(g34,g6) = 5
    c: DistanceY(g6,g34) = 5
    c: DistanceY(g33,g8) = 5
    c: Coincident(g38,g39)
    c: Coincident(g39,g40)
    c: Coincident(g40,g41)
    c: Coincident(g41,g38)
    c: Horizontal(g38)
    c: Horizontal(g40)
    c: Vertical(g39)
    c: Vertical(g41)
    c: Vertical(g39,g33)
    c: Vertical(g38,g-9)
    c: DistanceY(g38,g0) = 5
    c: DistanceY(g2,g39) = 5
FEATURE [PartDesign::Pad] Pad004
  BaseFeature = -> Pocket004
  Direction = (0,0,1)
  Length = 3
  Length2 = 10
  Profile = -> Sketch015
  ReferenceAxis = -> Sketch015 [N_Axis]
  TaperAngle = -30
  Type = 0
  UseCustomVector = true
FEATURE [Sketcher::SketchObject] Sketch016
  AttachmentOffset = pos=(0,0,15.4) rot=(0,0,1;0rad)
  ExternalGeometry = -> [Thickness001]
  FullyConstrained = true
  MapMode = 5
  Placement = pos=(0,0,15.4) rot=(0,0,1;0rad)
  Support = -> [Thickness001]
  expr: .AttachmentOffset.Base.z = <<data>>.lattepanda_height
  expr: Constraints[4] = Sketch005.Constraints[4]
  expr: Constraints[68] = Sketch005.Constraints[68]
  expr: Constraints[8] = Sketch005.Constraints[8]
  sketch-geometry (24):
    g0: LineSegment StartX=-59.5 StartY=39 StartZ=0 EndX=-55.7 EndY=39 EndZ=0
    g1: LineSegment StartX=-62.5 StartY=36 StartZ=0 EndX=-62.5 EndY=32.2 EndZ=0
    g2: LineSegment StartX=-55.7 StartY=39 StartZ=0 EndX=-55.7 EndY=35.6 EndZ=0
    g3: ArcOfCircle CenterX=-59.1 CenterY=35.6 CenterZ=0 NormalX=0 NormalY=0 NormalZ=1 AngleXU=0 Radius=3.4 StartAngle=4.71239 EndAngle=6.28319
    g4: LineSegment StartX=-62.5 StartY=32.2 StartZ=0 EndX=-59.1 EndY=32.2 EndZ=0
    g5: LineSegment StartX=-59.5 StartY=-39 StartZ=0 EndX=-55.7 EndY=-39 EndZ=0
    g6: LineSegment StartX=-62.5 StartY=-36 StartZ=0 EndX=-62.5 EndY=-32.2 EndZ=0
    g7: LineSegment StartX=-55.7 StartY=-39 StartZ=0 EndX=-55.7 EndY=-35.6 EndZ=0
    g8: ArcOfCircle CenterX=-59.1 CenterY=-35.6 CenterZ=0 NormalX=0 NormalY=0 NormalZ=1 AngleXU=0 Radius=3.4 StartAngle=-2.7e-15 EndAngle=1.5708
    g9: LineSegment StartX=-62.5 StartY=-32.2 StartZ=0 EndX=-59.1 EndY=-32.2 EndZ=0
    g10: LineSegment StartX=59.5 StartY=39 StartZ=0 EndX=55.7 EndY=39 EndZ=0
    g11: LineSegment StartX=62.5 StartY=36 StartZ=0 EndX=62.5 EndY=32.2 EndZ=0
    g12: LineSegment StartX=55.7 StartY=39 StartZ=0 EndX=55.7 EndY=35.6 EndZ=0
    g13: ArcOfCircle CenterX=59.1 CenterY=35.6 CenterZ=0 NormalX=0 NormalY=0 NormalZ=1 AngleXU=0 Radius=3.4 StartAngle=3.14159 EndAngle=4.71239
    g14: LineSegment StartX=62.5 StartY=32.2 StartZ=0 EndX=59.1 EndY=32.2 EndZ=0
    g15: LineSegment StartX=59.5 StartY=-39 StartZ=0 EndX=55.7 EndY=-39 EndZ=0
    g16: LineSegment StartX=62.5 StartY=-36 StartZ=0 EndX=62.5 EndY=-32.2 EndZ=0
    g17: LineSegment StartX=55.7 StartY=-39 StartZ=0 EndX=55.7 EndY=-35.6 EndZ=0
    g18: ArcOfCircle CenterX=59.1 CenterY=-35.6 CenterZ=0 NormalX=0 NormalY=0 NormalZ=1 AngleXU=0 Radius=3.4 StartAngle=1.5708 EndAngle=3.14159
    g19: LineSegment StartX=62.5 StartY=-32.2 StartZ=0 EndX=59.1 EndY=-32.2 EndZ=0
    g20: ArcOfCircle CenterX=-59.5 CenterY=-36 CenterZ=0 NormalX=0 NormalY=0 NormalZ=1 AngleXU=0 Radius=3 StartAngle=3.14159 EndAngle=4.71239
    g21: ArcOfCircle CenterX=-59.5 CenterY=36 CenterZ=0 NormalX=0 NormalY=0 NormalZ=1 AngleXU=0 Radius=3 StartAngle=1.5708 EndAngle=3.14159
    g22: ArcOfCircle CenterX=59.5 CenterY=36 CenterZ=0 NormalX=0 NormalY=0 NormalZ=1 AngleXU=0 Radius=3 StartAngle=2.089e-13 EndAngle=1.5708
    g23: ArcOfCircle CenterX=59.5 CenterY=-36 CenterZ=0 NormalX=0 NormalY=0 NormalZ=1 AngleXU=0 Radius=3 StartAngle=4.71239 EndAngle=6.28319
  constraints (72):
    c: Coincident(g0,g-3)
    c: Horizontal(g0)
    c: Coincident(g1,g-3)
    c: Vertical(g1)
    c: DistanceX(g1,g0) = 6.8
    c: Coincident(g2,g0)
    c: Vertical(g2)
    c: Coincident(g3,g2)
    c: Radius(g3) = 3.4
    c: Coincident(g4,g1)
    c: Coincident(g4,g3)
    c: Horizontal(g4)
    c: Equal(g1,g0)
    c: Equal(g4,g2)
    c: Horizontal(g5)
    c: Vertical(g6)
    c: Coincident(g7,g5)
    c: Vertical(g7)
    c: Coincident(g8,g7)
    c: Coincident(g9,g6)
    c: Coincident(g9,g8)
    c: Horizontal(g9)
    c: Equal(g6,g5)
    c: Equal(g9,g7)
    c: Coincident(g6,g-4)
    c: Coincident(g5,g-4)
    c: Equal(g6,g1)
    c: Equal(g9,g4)
    c: Horizontal(g10)
    c: Vertical(g11)
    c: Coincident(g12,g10)
    c: Vertical(g12)
    c: Coincident(g13,g12)
    c: Coincident(g14,g11)
    c: Coincident(g14,g13)
    c: Horizontal(g14)
    c: Equal(g11,g10)
    c: Equal(g14,g12)
    c: Horizontal(g15)
    c: Vertical(g16)
    c: Coincident(g17,g15)
    c: Vertical(g17)
    c: Coincident(g18,g17)
    c: Coincident(g19,g16)
    c: Coincident(g19,g18)
    c: Horizontal(g19)
    c: Equal(g16,g15)
    c: Equal(g19,g17)
    c: Equal(g16,g11)
    c: Equal(g19,g14)
    c: Coincident(g10,g-6)
    c: Coincident(g11,g-6)
    c: Coincident(g16,g-5)
    c: Coincident(g15,g-5)
    c: Equal(g10,g0)
    c: Coincident(g20,g-4)
    c: Coincident(g20,g5)
    c: Coincident(g20,g6)
    c: Coincident(g21,g-3)
    c: Coincident(g21,g1)
    c: Coincident(g21,g0)
    c: Coincident(g22,g-6)
    c: Coincident(g22,g10)
    c: Coincident(g22,g11)
    c: Coincident(g23,g-5)
    c: Coincident(g23,g16)
    c: Coincident(g23,g15)
    c: Equal(g17,g7)
    c: DistanceY(g2,g2) = 3.4
    c: Equal(g3,g13)
    c: Equal(g18,g8)
    c: Equal(g13,g18)
FEATURE [PartDesign::Pad] Pad005
  BaseFeature = -> Pad004
  Direction = (0,0,-1)
  Length = 9.2
  Length2 = 10
  Profile = -> Sketch016
  ReferenceAxis = -> Sketch016 [N_Axis]
  Type = 0
  UseCustomVector = true
  expr: Length = <<data>>.lattepanda_h_above
FEATURE [Sketcher::SketchObject] Sketch017
  ExternalGeometry = -> [Pad005]
  FullyConstrained = false
  MapMode = 5
  Placement = pos=(0,0,15.4) rot=(0,0,1;0rad)
  Support = -> [Pad005]
  sketch-geometry (10):
    g0: ArcOfCircle CenterX=-59.5 CenterY=36 CenterZ=0 NormalX=0 NormalY=0 NormalZ=1 AngleXU=0 Radius=5 StartAngle=1.5708 EndAngle=3.14159
    g1: LineSegment StartX=-59.5 StartY=41 StartZ=0 EndX=59.5 EndY=41 EndZ=0
    g2: ArcOfCircle CenterX=59.5 CenterY=36 CenterZ=0 NormalX=0 NormalY=0 NormalZ=1 AngleXU=0 Radius=5 StartAngle=5e-16 EndAngle=1.5708
    g3: LineSegment StartX=64.5 StartY=36 StartZ=0 EndX=64.5 EndY=-36 EndZ=0
    g4: ArcOfCircle CenterX=59.5 CenterY=-36 CenterZ=0 NormalX=0 NormalY=0 NormalZ=1 AngleXU=0 Radius=5 StartAngle=4.71239 EndAngle=6.28319
    g5: LineSegment StartX=59.5 StartY=-41 StartZ=0 EndX=-59.5 EndY=-41 EndZ=0
    g6: ArcOfCircle CenterX=-59.5 CenterY=-36 CenterZ=0 NormalX=0 NormalY=0 NormalZ=1 AngleXU=0 Radius=5 StartAngle=3.14159 EndAngle=4.71239
    g7: LineSegment StartX=-64.5 StartY=-36 StartZ=0 EndX=-64.5 EndY=36 EndZ=0
    g8: GeomPoint X=-64.5 Y=41 Z=0
    g9: GeomPoint X=64.5 Y=-41 Z=0
  constraints (20):
    c: Tangent(g0,g1) = 1.5708
    c: Tangent(g1,g2) = 1.5708
    c: Tangent(g2,g3) = 1.5708
    c: Tangent(g3,g4) = 1.5708
    c: Tangent(g4,g5) = 1.5708
    c: Tangent(g5,g6) = 1.5708
    c: Tangent(g6,g7) = 1.5708
    c: Tangent(g7,g0) = 1.5708
    c: Equal(g0,g2)
    c: Equal(g2,g4)
    c: Equal(g4,g6)
    c: PointOnObject(g8,g1)
    c: PointOnObject(g8,g7)
    c: PointOnObject(g9,g3)
    c: PointOnObject(g9,g5)
    c: Coincident(g3,g-6)
    c: Coincident(g-5,g4)
    c: Coincident(g2,g-7)
    c: Coincident(g5,g-5)
    c: Coincident(g0,g-4)
FEATURE [PartDesign::Pad] Pad006
  BaseFeature = -> Pad005
  Direction = (0,0,1)
  Length = 2
  Length2 = 10
  Profile = -> Sketch017
  ReferenceAxis = -> Sketch017 [N_Axis]
  Type = 0
  expr: Length = <<data>>.wall_thickness
FEATURE [Sketcher::SketchObject] Sketch020
  ExternalGeometry = -> [Feature]
  FullyConstrained = true
  MapMode = 5
  Placement = pos=(0,0,15.4) rot=(1,0,0;3.14159rad)
  Support = -> [Pad006]
  sketch-geometry (2):
    g0: Circle CenterX=12.5 CenterY=-3.0025e-10 CenterZ=0 NormalX=0 NormalY=0 NormalZ=1 AngleXU=0 Radius=18.5791
    g1: GeomPoint X=31.0791 Y=-3.0025e-10 Z=0
  constraints (5):
    c: Horizontal(g0,g-62)
    c: Vertical(g0,g-62)
    c: PointOnObject(g1,g0)
    c: DistanceX(g-62,g1) = 2
    c: Horizontal(g1,g-62)
FEATURE [PartDesign::Pocket] Pocket005
  BaseFeature = -> Pad006
  Direction = (0,0,1)
  Length = 5
  Length2 = 5
  Profile = -> Sketch020
  ReferenceAxis = -> Sketch020 [N_Axis]
  TaperAngle = 45
  Type = 0
FEATURE [Sketcher::SketchObject] Sketch021
  ExternalGeometry = -> [Feature]
  FullyConstrained = true
  MapMode = 5
  Placement = pos=(0,0,15.4) rot=(1,0,0;3.14159rad)
  Support = -> [Pocket005]
  sketch-geometry (13):
    g0: LineSegment StartX=-34.9225 StartY=-16.5493 StartZ=0 EndX=-41.3917 EndY=-21.4378 EndZ=0
    g1: LineSegment StartX=-41.3917 StartY=-21.4378 StartZ=0 EndX=-37.5778 EndY=-26.4484 EndZ=0
    g2: LineSegment StartX=-34.9225 StartY=16.5493 StartZ=0 EndX=-41.3917 EndY=21.4378 EndZ=0
    g3: LineSegment StartX=-41.3917 StartY=21.4378 StartZ=0 EndX=-37.5778 EndY=26.4484 EndZ=0
    g4: LineSegment StartX=-34.9225 StartY=16.5493 StartZ=0 EndX=-34.9225 EndY=-16.5493 EndZ=0
    g5: GeomPoint X=-55.55 Y=-27 Z=0
    g6: GeomPoint X=-55.55 Y=27 Z=0
    g7: LineSegment StartX=-55.55 StartY=27 StartZ=0 EndX=-37.5778 EndY=27 EndZ=0
    g8: LineSegment StartX=-55.55 StartY=27 StartZ=0 EndX=-55.55 EndY=-27 EndZ=0
    g9: LineSegment StartX=-37.5778 StartY=27 StartZ=0 EndX=-37.5778 EndY=26.4484 EndZ=0
    g10: GeomPoint X=-37.5778 Y=-27 Z=0
    g11: LineSegment StartX=-55.55 StartY=-27 StartZ=0 EndX=-37.5778 EndY=-27 EndZ=0
    g12: LineSegment StartX=-37.5778 StartY=-26.4484 StartZ=0 EndX=-37.5778 EndY=-27 EndZ=0
  constraints (25):
    c: Coincident(g0,g-41)
    c: Coincident(g0,g-42)
    c: Coincident(g1,g0)
    c: Coincident(g1,g-43)
    c: Coincident(g2,g-58)
    c: Coincident(g2,g-58)
    c: Coincident(g3,g2)
    c: Coincident(g3,g-57)
    c: Coincident(g4,g2)
    c: Coincident(g4,g0)
    c: Symmetric(g-66,g-5,g6)
    c: Symmetric(g-64,g-3,g5)
    c: Coincident(g7,g6)
    c: Horizontal(g7)
    c: Coincident(g8,g7)
    c: Coincident(g8,g5)
    c: Coincident(g9,g7)
    c: Coincident(g9,g3)
    c: Vertical(g9)
    c: Vertical(g10,g1)
    c: Horizontal(g10,g8)
    c: Coincident(g11,g8)
    c: Coincident(g11,g10)
    c: Coincident(g12,g1)
    c: Coincident(g12,g11)
FEATURE [PartDesign::Pocket] Pocket006
  BaseFeature = -> Pocket005
  Direction = (-1,0,1)
  Length = 5
  Length2 = 5
  Profile = -> Sketch021
  ReferenceAxis = -> Sketch021 [N_Axis]
  Type = 0
  UseCustomVector = true
FEATURE [Sketcher::SketchObject] Sketch022
  ExternalGeometry = -> [Feature]
  FullyConstrained = true
  MapMode = 5
  Placement = pos=(0,0,15.4) rot=(1,0,0;3.14159rad)
  Support = -> [Pocket006]
  sketch-geometry (9):
    g0: GeomPoint X=12.1912 Y=-2.02094e-11 Z=0
    g1: ArcOfCircle CenterX=12.1912 CenterY=-2.02094e-11 CenterZ=0 NormalX=0 NormalY=0 NormalZ=1 AngleXU=0 Radius=28.2773 StartAngle=5.29293 EndAngle=7.27344
    g2: ArcOfCircle CenterX=12.1912 CenterY=-2.02094e-11 CenterZ=0 NormalX=0 NormalY=0 NormalZ=1 AngleXU=0 Radius=42.9494 StartAngle=5.56505 EndAngle=7.00132
    g3: GeomPoint X=29.0791 Y=28.2598 Z=0
    g4: GeomPoint X=29.0791 Y=-28.2598 Z=0
    g5: LineSegment StartX=29.0791 StartY=28.2598 StartZ=0 EndX=44.5336 EndY=28.2598 EndZ=0
    g6: LineSegment StartX=29.0791 StartY=-28.2598 StartZ=0 EndX=44.5336 EndY=-28.2598 EndZ=0
    g7: ArcOfCircle CenterX=29.0791 CenterY=25.7463 CenterZ=0 NormalX=0 NormalY=0 NormalZ=1 AngleXU=0 Radius=2.51352 StartAngle=1.5708 EndAngle=4.13185
    g8: ArcOfCircle CenterX=29.0791 CenterY=-25.7463 CenterZ=0 NormalX=0 NormalY=0 NormalZ=1 AngleXU=0 Radius=2.51352 StartAngle=2.15133 EndAngle=4.71239
  constraints (20):
    c: Vertical(g0,g-47)
    c: Coincident(g1,g0)
    c: Coincident(g2,g1)
    c: PointOnObject(g-50,g2)
    c: Horizontal(g2,g-16)
    c: Horizontal(g2,g-20)
    c: Horizontal(g1,g-63)
    c: Vertical(g3,g4)
    c: Horizontal(g-16,g4)
    c: Horizontal(g3,g-20)
    c: Coincident(g5,g3)
    c: Coincident(g5,g2)
    c: Coincident(g6,g4)
    c: Coincident(g6,g2)
    c: Tangent(g7,g5) = 1.5708
    c: Tangent(g7,g1) = 1.5708
    c: Tangent(g8,g6) = -1.5708
    c: Tangent(g8,g1) = 1.5708
    c: PointOnObject(g-48,g1)
    c: Vertical(g8,g-62)
FEATURE [PartDesign::Pocket] Pocket007
  BaseFeature = -> Pocket006
  Direction = (1,0,1)
  Length = 5
  Length2 = 5
  Profile = -> Sketch022
  ReferenceAxis = -> Sketch022 [N_Axis]
  Type = 0
  UseCustomVector = true
FEATURE [Sketcher::SketchObject] Sketch023
  ExternalGeometry = -> [Pocket007]
  FullyConstrained = true
  MapMode = 5
  Placement = pos=(0,0,17.4) rot=(0,0,1;0rad)
  Support = -> [Pocket007]
  sketch-geometry (5):
    g0: GeomPoint X=-59 Y=-35.5 Z=0
    g1: Circle CenterX=-59 CenterY=-35.5 CenterZ=0 NormalX=0 NormalY=0 NormalZ=1 AngleXU=0 Radius=1.75
    g2: Circle CenterX=59 CenterY=-35.5 CenterZ=0 NormalX=0 NormalY=0 NormalZ=1 AngleXU=0 Radius=1.75
    g3: Circle CenterX=-59 CenterY=35.5 CenterZ=0 NormalX=0 NormalY=0 NormalZ=1 AngleXU=0 Radius=1.75
    g4: Circle CenterX=59 CenterY=35.5 CenterZ=0 NormalX=0 NormalY=0 NormalZ=1 AngleXU=0 Radius=1.75
  constraints (13):
    c: Coincident(g1,g0)
    c: Diameter(g1) = 3.5
    c: Diameter(g2) = 3.5
    c: Diameter(g3) = 3.5
    c: Diameter(g4) = 3.5
    c: DistanceX(g-6,g3) = 0.5
    c: DistanceY(g3,g-3) = 0.5
    c: Vertical(g3,g1)
    c: Horizontal(g3,g4)
    c: DistanceY(g-5,g2) = 0.5
    c: DistanceX(g2,g-4) = 0.5
    c: Horizontal(g1,g2)
    c: Vertical(g2,g4)
FEATURE [PartDesign::Hole] Hole
  BaseFeature = -> Pocket007
  CustomThreadClearance = 0
  Depth = 311.246
  DepthType = 1
  Diameter = 3.9
  DrillForDepth = false
  DrillPoint = 1
  DrillPointAngle = 118
  HoleCutCountersinkAngle = 90
  HoleCutCustomValues = false
  HoleCutDepth = 3.2
  HoleCutDiameter = 6.1
  HoleCutType = 1
  ModelThread = false
  Profile = -> Sketch023
  Tapered = false
  TaperedAngle = 90
  ThreadClass = 0
  ThreadDepth = 311.246
  ThreadDepthType = 0
  ThreadDirection = 0
  ThreadFit = 0
  ThreadSize = 10
  ThreadType = 1
  Threaded = false
  UseCustomThreadClearance = false
FEATURE [Sketcher::SketchObject] Sketch042
  ExternalGeometry = -> [Feature]
  FullyConstrained = true
  MapMode = 5
  Placement = pos=(0,0,17.4) rot=(0,0,1;0rad)
  Support = -> [Hole]
  sketch-geometry (4):
    g0: LineSegment StartX=40.75 StartY=-32.3 StartZ=0 EndX=52.75 EndY=-32.3 EndZ=0
    g1: LineSegment StartX=52.75 StartY=-32.3 StartZ=0 EndX=52.75 EndY=-37.7 EndZ=0
    g2: LineSegment StartX=52.75 StartY=-37.7 StartZ=0 EndX=40.75 EndY=-37.7 EndZ=0
    g3: LineSegment StartX=40.75 StartY=-37.7 StartZ=0 EndX=40.75 EndY=-32.3 EndZ=0
  constraints (10):
    c: Coincident(g0,g1)
    c: Coincident(g1,g2)
    c: Coincident(g2,g3)
    c: Coincident(g3,g0)
    c: Horizontal(g0)
    c: Horizontal(g2)
    c: Vertical(g1)
    c: Vertical(g3)
    c: Coincident(g0,g-3)
    c: Coincident(g1,g-4)
FEATURE [PartDesign::Pocket] Pocket014
  BaseFeature = -> Hole
  Direction = (0,0,-1)
  Length = 5
  Length2 = 5
  Profile = -> Sketch042
  ReferenceAxis = -> Sketch042 [N_Axis]
  Type = 0
FEATURE [PartDesign::Body] Body001  label="case"
  Group = -> [Sketch004,Pad002,Thickness001,Sketch005,Pad003,Sketch007,Pocket,Sketch009,Pocket001,Sketch010,Pocket002,Sketch012,Pocket003,Sketch014,Pocket004,Sketch015,Pad004,Sketch016,Pad005,Sketch017,Pad006,Sketch020,Pocket005,Sketch021,Pocket006,Sketch022,Pocket007,Sketch023,Hole,Sketch042,Pocket014]
  Origin = -> Origin001
  Tip = -> Pocket014
COMPONENT P2 — recipe-attached ("bottom_filter", modeled in this document).
Construction recipe (the document's own serialized feature program — sketch geometry with constraints, then the solid features built on it; lengths are millimeters unless a unit is written):

FEATURE [Sketcher::SketchObject] Sketch028
  FullyConstrained = true
  MapMode = 5
  Support = -> [XY_Plane006]
  expr: Constraints[8] = <<data>>.lattepanda_long + <<data>>.wall_thickness * 2
  expr: Constraints[9] = <<data>>.lattepanda_short + <<data>>.wall_thickness * 2
  sketch-geometry (4):
    g0: LineSegment StartX=-64.5 StartY=41 StartZ=0 EndX=64.5 EndY=41 EndZ=0
    g1: LineSegment StartX=64.5 StartY=41 StartZ=0 EndX=64.5 EndY=-41 EndZ=0
    g2: LineSegment StartX=64.5 StartY=-41 StartZ=0 EndX=-64.5 EndY=-41 EndZ=0
    g3: LineSegment StartX=-64.5 StartY=-41 StartZ=0 EndX=-64.5 EndY=41 EndZ=0
  constraints (11):
    c: Coincident(g0,g1)
    c: Coincident(g1,g2)
    c: Coincident(g2,g3)
    c: Coincident(g3,g0)
    c: Horizontal(g0)
    c: Horizontal(g2)
    c: Vertical(g1)
    c: Vertical(g3)
    c: DistanceX(g0,g0) = 129
    c: DistanceY(g1,g1) = 82
    c: Symmetric(g1,g0,g-1)
FEATURE [PartDesign::Pad] Pad009
  Direction = (0,0,1)
  Length = 2
  Length2 = 10
  Profile = -> Sketch028
  ReferenceAxis = -> Sketch028 [N_Axis]
  Reversed = true
  Type = 0
  expr: Length = <<data>>.wall_thickness
FEATURE [Sketcher::SketchObject] Sketch030
  ExternalGeometry = -> [Pad009]
  FullyConstrained = true
  MapMode = 5
  Support = -> [Pad009]
  expr: Constraints[10] = <<data>>.screwhole_shaft_diameter + Spreadsheet.padding * 2 + <<data>>.wall_thickness
  expr: Constraints[11] = <<data>>.screwhole_shaft_diameter + Spreadsheet.padding * 2 + <<data>>.wall_thickness
  expr: Constraints[8] = Sketch029.Constraints[8]
  sketch-geometry (4):
    g0: LineSegment StartX=-64.5 StartY=32.2 StartZ=0 EndX=-62.5 EndY=32.2 EndZ=0
    g1: LineSegment StartX=-62.5 StartY=32.2 StartZ=0 EndX=-62.5 EndY=-32.2 EndZ=0
    g2: LineSegment StartX=-62.5 StartY=-32.2 StartZ=0 EndX=-64.5 EndY=-32.2 EndZ=0
    g3: LineSegment StartX=-64.5 StartY=-32.2 StartZ=0 EndX=-64.5 EndY=32.2 EndZ=0
  constraints (12):
    c: Coincident(g0,g1)
    c: Coincident(g1,g2)
    c: Coincident(g2,g3)
    c: Coincident(g3,g0)
    c: Horizontal(g0)
    c: Horizontal(g2)
    c: Vertical(g1)
    c: Vertical(g3)
    c: DistanceX(g0,g0) = 2
    c: PointOnObject(g0,g-3)
    c: DistanceY(g0,g-3) = 8.8
    c: DistanceY(g-3,g2) = 8.8
FEATURE [PartDesign::Pad] Pad010
  BaseFeature = -> Pad009
  Direction = (0,0,1)
  Length = 10
  Length2 = 10
  Profile = -> Sketch030
  ReferenceAxis = -> Sketch030 [N_Axis]
  Type = 0
FEATURE [Sketcher::SketchObject] Sketch031
  ExternalGeometry = -> [Pad010]
  FullyConstrained = true
  MapMode = 5
  Support = -> [Pad010]
  expr: Constraints[10] = <<data>>.screwhole_shaft_diameter + Spreadsheet.padding * 2 + <<data>>.wall_thickness
  expr: Constraints[11] = <<data>>.screwhole_shaft_diameter + Spreadsheet.padding * 2 + <<data>>.wall_thickness
  expr: Constraints[9] = <<data>>.wall_thickness
  sketch-geometry (4):
    g0: LineSegment StartX=64.5 StartY=32.2 StartZ=0 EndX=62.5 EndY=32.2 EndZ=0
    g1: LineSegment StartX=62.5 StartY=32.2 StartZ=0 EndX=62.5 EndY=-32.2 EndZ=0
    g2: LineSegment StartX=62.5 StartY=-32.2 StartZ=0 EndX=64.5 EndY=-32.2 EndZ=0
    g3: LineSegment StartX=64.5 StartY=-32.2 StartZ=0 EndX=64.5 EndY=32.2 EndZ=0
  constraints (12):
    c: Coincident(g0,g1)
    c: Coincident(g1,g2)
    c: Coincident(g2,g3)
    c: Coincident(g3,g0)
    c: Horizontal(g0)
    c: Horizontal(g2)
    c: Vertical(g1)
    c: Vertical(g3)
    c: PointOnObject(g0,g-3)
    c: DistanceX(g0,g0) = 2
    c: DistanceY(g0,g-3) = 8.8
    c: DistanceY(g-3,g2) = 8.8
FEATURE [PartDesign::Pad] Pad011
  BaseFeature = -> Pad010
  Direction = (0,0,1)
  Length = 8.4
  Length2 = 10
  Profile = -> Sketch031
  ReferenceAxis = -> Sketch031 [N_Axis]
  Type = 0
FEATURE [Sketcher::SketchObject] Sketch032
  ExternalGeometry = -> [Pad011]
  FullyConstrained = true
  MapMode = 5
  Support = -> [Pad011]
  expr: Constraints[10] = <<data>>.screwhole_shaft_diameter + Spreadsheet.padding * 2 + <<data>>.wall_thickness
  expr: Constraints[11] = <<data>>.wall_thickness
  expr: Constraints[9] = <<data>>.screwhole_shaft_diameter + Spreadsheet.padding * 2 + <<data>>.wall_thickness
  sketch-geometry (4):
    g0: LineSegment StartX=-55.7 StartY=-41 StartZ=0 EndX=55.7 EndY=-41 EndZ=0
    g1: LineSegment StartX=55.7 StartY=-41 StartZ=0 EndX=55.7 EndY=-39 EndZ=0
    g2: LineSegment StartX=55.7 StartY=-39 StartZ=0 EndX=-55.7 EndY=-39 EndZ=0
    g3: LineSegment StartX=-55.7 StartY=-39 StartZ=0 EndX=-55.7 EndY=-41 EndZ=0
  constraints (12):
    c: Coincident(g0,g1)
    c: Coincident(g1,g2)
    c: Coincident(g2,g3)
    c: Coincident(g3,g0)
    c: Horizontal(g0)
    c: Horizontal(g2)
    c: Vertical(g1)
    c: Vertical(g3)
    c: PointOnObject(g0,g-3)
    c: DistanceX(g0,g-3) = 8.8
    c: DistanceX(g-3,g0) = 8.8
    c: DistanceY(g1,g1) = 2
FEATURE [PartDesign::Pad] Pad012
  BaseFeature = -> Pad011
  Direction = (0,0,1)
  Length = 4.3
  Length2 = 10
  Profile = -> Sketch032
  ReferenceAxis = -> Sketch032 [N_Axis]
  Type = 0
FEATURE [Sketcher::SketchObject] Sketch033
  ExternalGeometry = -> [Pad012]
  FullyConstrained = true
  MapMode = 5
  Support = -> [Pad012]
  expr: Constraints[10] = <<data>>.screwhole_shaft_diameter + Spreadsheet.padding * 2 + <<data>>.wall_thickness
  expr: Constraints[11] = <<data>>.wall_thickness
  sketch-geometry (4):
    g0: LineSegment StartX=-55.7 StartY=41 StartZ=0 EndX=0 EndY=41 EndZ=0
    g1: LineSegment StartX=0 StartY=41 StartZ=0 EndX=0 EndY=39 EndZ=0
    g2: LineSegment StartX=0 StartY=39 StartZ=0 EndX=-55.7 EndY=39 EndZ=0
    g3: LineSegment StartX=-55.7 StartY=39 StartZ=0 EndX=-55.7 EndY=41 EndZ=0
  constraints (12):
    c: Coincident(g0,g1)
    c: Coincident(g1,g2)
    c: Coincident(g2,g3)
    c: Coincident(g3,g0)
    c: Horizontal(g0)
    c: Horizontal(g2)
    c: Vertical(g1)
    c: Vertical(g3)
    c: PointOnObject(g0,g-3)
    c: PointOnObject(g1,g-2)
    c: DistanceX(g-3,g0) = 8.8
    c: DistanceY(g3,g3) = 2
FEATURE [PartDesign::Pad] Pad013
  BaseFeature = -> Pad012
  Direction = (0,0,1)
  Length = 4.8
  Length2 = 10
  Profile = -> Sketch033
  ReferenceAxis = -> Sketch033 [N_Axis]
  Type = 0
FEATURE [Sketcher::SketchObject] Sketch034
  ExternalGeometry = -> [Pad013]
  FullyConstrained = true
  MapMode = 5
  Support = -> [Pad013]
  expr: Constraints[10] = <<data>>.screwhole_shaft_diameter + Spreadsheet.padding * 2 + <<data>>.wall_thickness
  expr: Constraints[11] = <<data>>.wall_thickness
  sketch-geometry (4):
    g0: LineSegment StartX=55.7 StartY=41 StartZ=0 EndX=0 EndY=41 EndZ=0
    g1: LineSegment StartX=0 StartY=41 StartZ=0 EndX=0 EndY=39 EndZ=0
    g2: LineSegment StartX=0 StartY=39 StartZ=0 EndX=55.7 EndY=39 EndZ=0
    g3: LineSegment StartX=55.7 StartY=39 StartZ=0 EndX=55.7 EndY=41 EndZ=0
  constraints (12):
    c: Coincident(g0,g1)
    c: Coincident(g1,g2)
    c: Coincident(g2,g3)
    c: Coincident(g3,g0)
    c: Horizontal(g0)
    c: Horizontal(g2)
    c: Vertical(g1)
    c: Vertical(g3)
    c: PointOnObject(g0,g-3)
    c: PointOnObject(g1,g-2)
    c: DistanceX(g0,g-3) = 8.8
    c: DistanceY(g3,g3) = 2
FEATURE [PartDesign::Pad] Pad014
  BaseFeature = -> Pad013
  Direction = (0,0,1)
  Length = 7.4
  Length2 = 10
  Profile = -> Sketch034
  ReferenceAxis = -> Sketch034 [N_Axis]
  Type = 0
FEATURE [Sketcher::SketchObject] Sketch035
  ExternalGeometry = -> [Pad014]
  FullyConstrained = true
  MapMode = 5
  Placement = pos=(0,32.2,0) rot=(0,0.707107,0.707107;3.14159rad)
  Support = -> [Pad014]
  sketch-geometry (3):
    g0: LineSegment StartX=-64.5 StartY=8.4 StartZ=0 EndX=-62.5 EndY=8.4 EndZ=0
    g1: LineSegment StartX=-63.5 StartY=7.82265 StartZ=0 EndX=-62.5 EndY=8.4 EndZ=0
    g2: LineSegment StartX=-63.5 StartY=7.82265 StartZ=0 EndX=-64.5 EndY=8.4 EndZ=0
  constraints (7):
    c: Coincident(g0,g-3)
    c: Coincident(g0,g-3)
    c: Coincident(g1,g0)
    c: Coincident(g2,g1)
    c: Coincident(g2,g0)
    c: Equal(g2,g1)
    c: Angle(g0,g1) = 0.523599
FEATURE [PartDesign::Pocket] Pocket009
  BaseFeature = -> Pad014
  Direction = (0,-1,2e-16)
  Length = 10000
  Length2 = 5
  Profile = -> Sketch035
  ReferenceAxis = -> Sketch035 [N_Axis]
  Type = 0
FEATURE [Sketcher::SketchObject] Sketch036
  ExternalGeometry = -> [Pocket009]
  FullyConstrained = true
  MapMode = 5
  Placement = pos=(55.7,0,0) rot=(0.57735,0.57735,0.57735;2.0944rad)
  Support = -> [Pocket009]
  sketch-geometry (3):
    g0: LineSegment StartX=-41 StartY=4.3 StartZ=0 EndX=-39 EndY=4.3 EndZ=0
    g1: LineSegment StartX=-39 StartY=4.3 StartZ=0 EndX=-40 EndY=3.72265 EndZ=0
    g2: LineSegment StartX=-40 StartY=3.72265 StartZ=0 EndX=-41 EndY=4.3 EndZ=0
  constraints (7):
    c: Coincident(g0,g-3)
    c: Coincident(g0,g-3)
    c: Coincident(g2,g0)
    c: Equal(g2,g1)
    c: Coincident(g2,g1)
    c: Coincident(g1,g0)
    c: Angle(g0,g1) = 0.523599
FEATURE [PartDesign::Pocket] Pocket010
  BaseFeature = -> Pocket009
  Direction = (-1,0,0)
  Length = 1000
  Length2 = 5
  Profile = -> Sketch036
  ReferenceAxis = -> Sketch036 [N_Axis]
  Type = 0
FEATURE [Sketcher::SketchObject] Sketch037
  ExternalGeometry = -> [Pocket010]
  FullyConstrained = true
  MapMode = 5
  Placement = pos=(0,-32.2,0) rot=(1,0,0;1.5708rad)
  Support = -> [Pocket010]
  sketch-geometry (3):
    g0: LineSegment StartX=-64.5 StartY=10 StartZ=0 EndX=-62.5 EndY=10 EndZ=0
    g1: LineSegment StartX=-62.5 StartY=10 StartZ=0 EndX=-63.5 EndY=9.42265 EndZ=0
    g2: LineSegment StartX=-63.5 StartY=9.42265 StartZ=0 EndX=-64.5 EndY=10 EndZ=0
  constraints (7):
    c: Coincident(g0,g-3)
    c: Coincident(g0,g-3)
    c: Coincident(g1,g0)
    c: Coincident(g2,g1)
    c: Coincident(g2,g0)
    c: Equal(g2,g1)
    c: Angle(g0,g1) = 0.523599
FEATURE [PartDesign::Pocket] Pocket011
  BaseFeature = -> Pocket010
  Direction = (0,1,-2e-16)
  Length = 1000
  Length2 = 5
  Profile = -> Sketch037
  ReferenceAxis = -> Sketch037 [N_Axis]
  Type = 0
FEATURE [Sketcher::SketchObject] Sketch038
  ExternalGeometry = -> [Pocket011]
  FullyConstrained = true
  MapMode = 5
  Placement = pos=(55.7,0,0) rot=(0.57735,0.57735,0.57735;2.0944rad)
  Support = -> [Pocket011]
  sketch-geometry (3):
    g0: LineSegment StartX=39 StartY=7.4 StartZ=0 EndX=41 EndY=7.4 EndZ=0
    g1: LineSegment StartX=41 StartY=7.4 StartZ=0 EndX=40 EndY=6.82265 EndZ=0
    g2: LineSegment StartX=40 StartY=6.82265 StartZ=0 EndX=39 EndY=7.4 EndZ=0
  constraints (7):
    c: Coincident(g0,g-3)
    c: Coincident(g0,g-3)
    c: Coincident(g1,g0)
    c: Coincident(g2,g1)
    c: Coincident(g2,g0)
    c: Equal(g1,g2)
    c: Angle(g0,g1) = 0.523599
FEATURE [PartDesign::Pocket] Pocket012
  BaseFeature = -> Pocket011
  Direction = (-1,0,0)
  Length = 1000
  Length2 = 5
  Profile = -> Sketch038
  ReferenceAxis = -> Sketch038 [N_Axis]
  Type = 0
FEATURE [Sketcher::SketchObject] Sketch039
  ExternalGeometry = -> [Pocket012]
  FullyConstrained = true
  MapMode = 5
  Placement = pos=(-55.7,0,0) rot=(0.57735,-0.57735,-0.57735;2.0944rad)
  Support = -> [Pocket012]
  sketch-geometry (3):
    g0: LineSegment StartX=-41 StartY=4.8 StartZ=0 EndX=-39 EndY=4.8 EndZ=0
    g1: LineSegment StartX=-39 StartY=4.8 StartZ=0 EndX=-40 EndY=4.22265 EndZ=0
    g2: LineSegment StartX=-40 StartY=4.22265 StartZ=0 EndX=-41 EndY=4.8 EndZ=0
  constraints (7):
    c: Coincident(g0,g-3)
    c: Coincident(g0,g-3)
    c: Coincident(g1,g0)
    c: Coincident(g2,g1)
    c: Coincident(g2,g0)
    c: Equal(g2,g1)
    c: Angle(g0,g1) = 0.523599
FEATURE [PartDesign::Pocket] Pocket013
  BaseFeature = -> Pocket012
  Direction = (1,0,0)
  Length = 55.7
  Length2 = 5
  Profile = -> Sketch039
  ReferenceAxis = -> Sketch039 [N_Axis]
  Type = 0
  expr: Length = <<data>>.lattepanda_long / 2 - (<<data>>.screwhole_shaft_diameter + Spreadsheet.padding * 2)
FEATURE [Sketcher::SketchObject] Sketch040
  ExternalGeometry = -> [Pocket013]
  FullyConstrained = true
  MapMode = 5
  Support = -> [Pocket013]
  sketch-geometry (16):
    g0: LineSegment StartX=55.7 StartY=41 StartZ=0 EndX=64.5 EndY=41 EndZ=0
    g1: LineSegment StartX=64.5 StartY=41 StartZ=0 EndX=64.5 EndY=32.2 EndZ=0
    g2: LineSegment StartX=64.5 StartY=32.2 StartZ=0 EndX=55.7 EndY=32.2 EndZ=0
    g3: LineSegment StartX=55.7 StartY=32.2 StartZ=0 EndX=55.7 EndY=41 EndZ=0
    g4: LineSegment StartX=-55.7 StartY=41 StartZ=0 EndX=-64.5 EndY=41 EndZ=0
    g5: LineSegment StartX=-64.5 StartY=41 StartZ=0 EndX=-64.5 EndY=32.2 EndZ=0
    g6: LineSegment StartX=-64.5 StartY=32.2 StartZ=0 EndX=-55.7 EndY=32.2 EndZ=0
    g7: LineSegment StartX=-55.7 StartY=32.2 StartZ=0 EndX=-55.7 EndY=41 EndZ=0
    g8: LineSegment StartX=-64.5 StartY=-32.2 StartZ=0 EndX=-55.7 EndY=-32.2 EndZ=0
    g9: LineSegment StartX=-55.7 StartY=-32.2 StartZ=0 EndX=-55.7 EndY=-41 EndZ=0
    g10: LineSegment StartX=-55.7 StartY=-41 StartZ=0 EndX=-64.5 EndY=-41 EndZ=0
    g11: LineSegment StartX=-64.5 StartY=-41 StartZ=0 EndX=-64.5 EndY=-32.2 EndZ=0
    g12: LineSegment StartX=55.7 StartY=-41 StartZ=0 EndX=64.5 EndY=-41 EndZ=0
    g13: LineSegment StartX=64.5 StartY=-41 StartZ=0 EndX=64.5 EndY=-32.2 EndZ=0
    g14: LineSegment StartX=64.5 StartY=-32.2 StartZ=0 EndX=55.7 EndY=-32.2 EndZ=0
    g15: LineSegment StartX=55.7 StartY=-32.2 StartZ=0 EndX=55.7 EndY=-41 EndZ=0
  constraints (40):
    c: Coincident(g0,g1)
    c: Coincident(g1,g2)
    c: Coincident(g2,g3)
    c: Coincident(g3,g0)
    c: Horizontal(g0)
    c: Horizontal(g2)
    c: Vertical(g1)
    c: Vertical(g3)
    c: Coincident(g0,g-9)
    c: Coincident(g1,g-10)
    c: Coincident(g4,g5)
    c: Coincident(g5,g6)
    c: Coincident(g6,g7)
    c: Coincident(g7,g4)
    c: Horizontal(g4)
    c: Horizontal(g6)
    c: Vertical(g5)
    c: Vertical(g7)
    c: Coincident(g4,g-4)
    c: Coincident(g5,g-3)
    c: Coincident(g8,g9)
    c: Coincident(g9,g10)
    c: Coincident(g10,g11)
    c: Coincident(g11,g8)
    c: Horizontal(g8)
    c: Horizontal(g10)
    c: Vertical(g9)
    c: Vertical(g11)
    c: Coincident(g8,g-5)
    c: Coincident(g9,g-6)
    c: Coincident(g12,g13)
    c: Coincident(g13,g14)
    c: Coincident(g14,g15)
    c: Coincident(g15,g12)
    c: Horizontal(g12)
    c: Horizontal(g14)
    c: Vertical(g13)
    c: Vertical(g15)
    c: Coincident(g12,g-7)
    c: Coincident(g13,g-8)
FEATURE [PartDesign::Pad] Pad015
  BaseFeature = -> Pocket013
  Direction = (0,0,1)
  Length = 5.6
  Length2 = 10
  Profile = -> Sketch040
  ReferenceAxis = -> Sketch040 [N_Axis]
  Type = 0
  expr: Length = <<data>>.lattepanda_h_below + <<data>>.lattepanda_h_pcb / 2
FEATURE [PartDesign::Pad] Pad016
  BaseFeature = -> Pad015
  Direction = (0,0,1)
  Length = 2
  Length2 = 10
  Profile = -> Pad015 [Face34]
  Type = 0
  expr: Length = <<data>>.wall_thickness
FEATURE [PartDesign::Body] Body004  label="bottom_filter"
  Group = -> [Sketch028,Pad009,Sketch030,Pad010,Sketch031,Pad011,Sketch032,Pad012,Sketch033,Pad013,Sketch034,Pad014,Sketch035,Pocket009,Sketch036,Pocket010,Sketch037,Pocket011,Sketch038,Pocket012,Sketch039,Pocket013,Sketch040,Pad015,Pad016]
  Origin = -> Origin005
  Tip = -> Pad016
COMPONENT P3 — recipe-attached ("prototype_filter", modeled in this document).
Construction recipe (the document's own serialized feature program — sketch geometry with constraints, then the solid features built on it; lengths are millimeters unless a unit is written):

FEATURE [Sketcher::SketchObject] Sketch041
  FullyConstrained = false
  Placement = pos=(0,0,-20) rot=(0,0,1;0rad)
  sketch-geometry (4):
    g0: LineSegment StartX=67.998 StartY=-43.0439 StartZ=0 EndX=49.126 EndY=-43.0439 EndZ=0
    g1: LineSegment StartX=49.126 StartY=-43.0439 StartZ=0 EndX=49.126 EndY=43.1013 EndZ=0
    g2: LineSegment StartX=49.126 StartY=43.1013 StartZ=0 EndX=67.998 EndY=43.1013 EndZ=0
    g3: LineSegment StartX=67.998 StartY=43.1013 StartZ=0 EndX=67.998 EndY=-43.0439 EndZ=0
  constraints (8):
    c: Coincident(g0,g1)
    c: Coincident(g1,g2)
    c: Coincident(g2,g3)
    c: Coincident(g3,g0)
    c: Horizontal(g0)
    c: Horizontal(g2)
    c: Vertical(g1)
    c: Vertical(g3)
FEATURE [PartDesign::Pad] Pad017  label="Pad019"
  Direction = (0,0,1)
  Length = 50
  Length2 = 10
  Placement = pos=(0,0,-20) rot=(0,0,1;0rad)
  Profile = -> Sketch041
  ReferenceAxis = -> Sketch041 [N_Axis]
  Type = 0
FEATURE [PartDesign::Body] Body005  label="prototype_filter"
  Group = -> [Sketch041,Pad017]
  Origin = -> Origin006
  Placement = pos=(0,0,-10) rot=(0,0,1;0rad)
  Tip = -> Pad017
COMPONENT P4 — geometry summary ("Hole001"; no construction recipe available for this part):
  bounding box: 129.0 x 82.0 x 19.4 mm
  tessellated surface: 11,756 triangles
  volume: 44542 mm^3 (22% of its bounding box)
COMPONENT P5 — geometry summary ("Pad017"; no construction recipe available for this part):
  bounding box: 129.0 x 82.0 x 12.0 mm
  tessellated surface: 158 triangles
  volume: 46505 mm^3 (37% of its bounding box)
COMPONENT P6 — geometry summary ("Hole002"; no construction recipe available for this part):
  bounding box: 129.0 x 82.0 x 19.4 mm
  tessellated surface: 11,756 triangles
  volume: 44542 mm^3 (22% of its bounding box)
COMPONENT P7 — geometry summary ("Pad018"; no construction recipe available for this part):
  bounding box: 129.0 x 82.0 x 12.0 mm
  tessellated surface: 158 triangles
  volume: 46505 mm^3 (37% of its bounding box)
COMPONENT P8 — geometry summary ("top001"; no construction recipe available for this part):
  bounding box: 129.0 x 82.0 x 13.7 mm
  tessellated surface: 8,694 triangles
  volume: 22119 mm^3 (15% of its bounding box)
COMPONENT P9 — geometry summary ("bottom001"; no construction recipe available for this part):
  bounding box: 129.0 x 82.0 x 12.0 mm
  tessellated surface: 5,390 triangles
  volume: 22423 mm^3 (18% of its bounding box)
PROVENANCE & LICENSES
A FreeCAD (.FCStd) document from a public repository crawl; recipes are the document's own serialized feature recipes (and, for linked parts, companion documents' recipes).
License: as declared in the source repository (recorded in the dataset sidecar).
